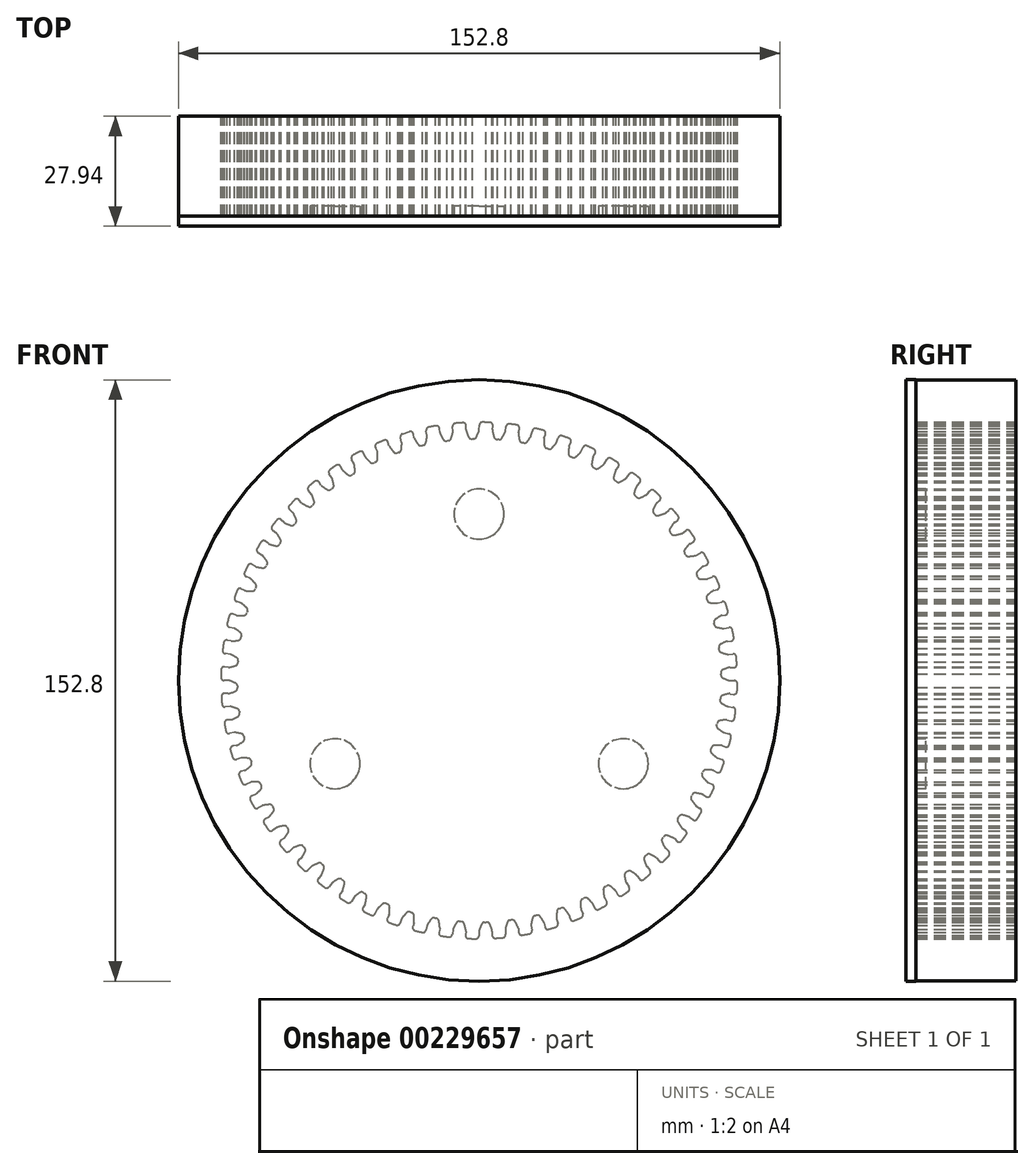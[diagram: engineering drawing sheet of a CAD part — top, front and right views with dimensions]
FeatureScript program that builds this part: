
annotation { "Feature Type Name" : "Feature", "Feature Type Description" : "" }
export const myFeature = defineFeature(function(context is Context, id is Id, definition is map)
    precondition{}
    {
        {
            var Q0;
            Q0=qCreatedBy(makeId("Front.planeOp"),FACE);
            var sketch = newSketch(context, id + "F0", { "sketchPlane" : qUnion([Q0])});
            skArc(sketch, "E0", {"start": v(-4.13, 65.49) * mm, "mid": v(-5.08, 65.42) * mm, "end": v(-6.03, 65.34) * mm});
            skPoint(sketch, "E1.orphan", {"position": v(-3.22, 59.34) * mm});
            skPoint(sketch, "E2.orphan", {"position": v(0.1, 59.43) * mm});
            skArc(sketch, "E3.MirrorCS", {"start": v(-3.28, 63.46) * mm, "mid": v(-3.01, 62.67) * mm, "end": v(-2.71, 61.9) * mm});
            skLineSegment(sketch, "E4.MirrorCS", {"start": v(-2.02, 61.41) * mm, "end": v(-1.72, 61.4) * mm});
            skLineSegment(sketch, "E5.MirrorCS", {"start": v(-1.42, 61.4) * mm, "end": v(-1.72, 61.4) * mm});
            skArc(sketch, "E6.MirrorCS", {"start": v(-0.05, 63.37) * mm, "mid": v(-0.36, 62.6) * mm, "end": v(-0.7, 61.84) * mm});
            skLineSegment(sketch, "E7.MirrorCS", {"start": v(-3.32, 63.72) * mm, "end": v(-3.3, 64.68) * mm});
            skLineSegment(sketch, "E8.MirrorCS", {"start": v(0, 63.63) * mm, "end": v(0.04, 64.84) * mm});
            skPoint(sketch, "E9.orphan", {"position": v(-2.51, 65.57) * mm});
            skPoint(sketch, "E10.MirrorCS.end.orphan", {"position": v(-3.27, 61.3) * mm});
            skPoint(sketch, "E10.MirrorCS.start.orphan", {"position": v(-3.32, 63.41) * mm});
            skPoint(sketch, "E11.end.orphan", {"position": v(0.06, 61.38) * mm});
            skPoint(sketch, "E12.trimOffspring.start.orphan", {"position": v(0, 63.5) * mm});
            skPoint(sketch, "E13.end.orphan", {"position": v(-1.72, 65.6) * mm});
            skPoint(sketch, "E13.start.orphan", {"position": v(-0.92, 65.61) * mm});
            skPoint(sketch, "E14.visualSharp", {"position": v(0.06, 65.62) * mm});
            skArc(sketch, "E14.filletArc", {"start": v(0.83, 65.61) * mm, "mid": v(0.28, 65.4) * mm, "end": v(0.04, 64.84) * mm});
            skPoint(sketch, "E15.visualSharp", {"position": v(-3.27, 65.54) * mm});
            skArc(sketch, "E15.filletArc", {"start": v(-3.3, 64.68) * mm, "mid": v(-3.54, 65.27) * mm, "end": v(-4.13, 65.49) * mm});
            skPoint(sketch, "E16.visualSharp", {"position": v(-2.51, 61.43) * mm});
            skArc(sketch, "E16.filletArc", {"start": v(-2.71, 61.9) * mm, "mid": v(-2.43, 61.55) * mm, "end": v(-2.02, 61.41) * mm});
            skPoint(sketch, "E17.visualSharp", {"position": v(-0.92, 61.39) * mm});
            skArc(sketch, "E17.filletArc", {"start": v(-1.42, 61.4) * mm, "mid": v(-1, 61.51) * mm, "end": v(-0.7, 61.84) * mm});
            skArc(sketch, "E18.filletArc", {"start": v(-0.05, 63.37) * mm, "mid": v(-0.01, 63.5) * mm, "end": v(0, 63.63) * mm});
            skPoint(sketch, "E19.visualSharp", {"position": v(-3.32, 63.59) * mm});
            skArc(sketch, "E19.filletArc", {"start": v(-3.32, 63.72) * mm, "mid": v(-3.31, 63.59) * mm, "end": v(-3.28, 63.46) * mm});
            skArc(sketch, "E20.1.0", {"start": v(-10.04, 63.98) * mm, "mid": v(-10.34, 64.54) * mm, "end": v(-10.95, 64.7) * mm});
            skLineSegment(sketch, "E20.1.1", {"start": v(-9.96, 63.02) * mm, "end": v(-10.04, 63.98) * mm});
            skArc(sketch, "E20.1.2", {"start": v(-9.96, 63.02) * mm, "mid": v(-9.94, 62.9) * mm, "end": v(-9.9, 62.77) * mm});
            skArc(sketch, "E20.1.3", {"start": v(-9.9, 62.77) * mm, "mid": v(-9.55, 62.01) * mm, "end": v(-9.17, 61.27) * mm});
            skArc(sketch, "E20.1.4", {"start": v(-9.17, 61.27) * mm, "mid": v(-8.86, 60.96) * mm, "end": v(-8.42, 60.87) * mm});
            skLineSegment(sketch, "E20.1.5", {"start": v(-8.42, 60.87) * mm, "end": v(-8.13, 60.89) * mm});
            skLineSegment(sketch, "E20.1.6", {"start": v(-7.83, 60.91) * mm, "end": v(-8.13, 60.89) * mm});
            skArc(sketch, "E20.1.7", {"start": v(-7.83, 60.91) * mm, "mid": v(-7.42, 61.07) * mm, "end": v(-7.16, 61.43) * mm});
            skArc(sketch, "E20.1.8", {"start": v(-6.67, 63.02) * mm, "mid": v(-6.9, 62.22) * mm, "end": v(-7.16, 61.43) * mm});
            skArc(sketch, "E20.1.9", {"start": v(-6.67, 63.02) * mm, "mid": v(-6.65, 63.15) * mm, "end": v(-6.65, 63.28) * mm});
            skLineSegment(sketch, "E20.1.10", {"start": v(-6.65, 63.28) * mm, "end": v(-6.74, 64.5) * mm});
            skArc(sketch, "E20.1.11", {"start": v(-6.03, 65.34) * mm, "mid": v(-6.56, 65.06) * mm, "end": v(-6.74, 64.5) * mm});
            skArc(sketch, "E20.2.0", {"start": v(-16.67, 62.58) * mm, "mid": v(-17.03, 63.1) * mm, "end": v(-17.66, 63.2) * mm});
            skLineSegment(sketch, "E20.2.1", {"start": v(-16.5, 61.64) * mm, "end": v(-16.67, 62.58) * mm});
            skArc(sketch, "E20.2.2", {"start": v(-16.5, 61.64) * mm, "mid": v(-16.46, 61.5) * mm, "end": v(-16.4, 61.4) * mm});
            skArc(sketch, "E20.2.3", {"start": v(-16.4, 61.4) * mm, "mid": v(-15.98, 60.68) * mm, "end": v(-15.52, 59.98) * mm});
            skArc(sketch, "E20.2.4", {"start": v(-15.52, 59.98) * mm, "mid": v(-15.18, 59.7) * mm, "end": v(-14.74, 59.65) * mm});
            skLineSegment(sketch, "E20.2.5", {"start": v(-14.74, 59.65) * mm, "end": v(-14.45, 59.7) * mm});
            skLineSegment(sketch, "E20.2.6", {"start": v(-14.15, 59.76) * mm, "end": v(-14.45, 59.7) * mm});
            skArc(sketch, "E20.2.7", {"start": v(-14.15, 59.76) * mm, "mid": v(-13.76, 59.96) * mm, "end": v(-13.54, 60.35) * mm});
            skArc(sketch, "E20.2.8", {"start": v(-13.22, 61.98) * mm, "mid": v(-13.36, 61.16) * mm, "end": v(-13.54, 60.35) * mm});
            skArc(sketch, "E20.2.9", {"start": v(-13.22, 61.98) * mm, "mid": v(-13.21, 62.11) * mm, "end": v(-13.23, 62.24) * mm});
            skLineSegment(sketch, "E20.2.10", {"start": v(-13.23, 62.24) * mm, "end": v(-13.45, 63.43) * mm});
            skArc(sketch, "E20.2.11", {"start": v(-12.83, 64.35) * mm, "mid": v(-13.33, 64.02) * mm, "end": v(-13.45, 63.43) * mm});
            skArc(sketch, "E20.3.0", {"start": v(-23.12, 60.5) * mm, "mid": v(-23.53, 60.98) * mm, "end": v(-24.17, 61) * mm});
            skLineSegment(sketch, "E20.3.1", {"start": v(-22.85, 59.57) * mm, "end": v(-23.12, 60.5) * mm});
            skArc(sketch, "E20.3.2", {"start": v(-22.85, 59.57) * mm, "mid": v(-22.8, 59.45) * mm, "end": v(-22.73, 59.34) * mm});
            skArc(sketch, "E20.3.3", {"start": v(-22.73, 59.34) * mm, "mid": v(-22.23, 58.67) * mm, "end": v(-21.7, 58.03) * mm});
            skArc(sketch, "E20.3.4", {"start": v(-21.7, 58.03) * mm, "mid": v(-21.34, 57.79) * mm, "end": v(-20.9, 57.78) * mm});
            skLineSegment(sketch, "E20.3.5", {"start": v(-20.9, 57.78) * mm, "end": v(-20.6, 57.87) * mm});
            skLineSegment(sketch, "E20.3.6", {"start": v(-20.32, 57.95) * mm, "end": v(-20.6, 57.87) * mm});
            skArc(sketch, "E20.3.7", {"start": v(-20.32, 57.95) * mm, "mid": v(-19.95, 58.2) * mm, "end": v(-19.78, 58.6) * mm});
            skArc(sketch, "E20.3.8", {"start": v(-19.63, 60.26) * mm, "mid": v(-19.68, 59.43) * mm, "end": v(-19.78, 58.6) * mm});
            skArc(sketch, "E20.3.9", {"start": v(-19.63, 60.26) * mm, "mid": v(-19.63, 60.39) * mm, "end": v(-19.66, 60.52) * mm});
            skLineSegment(sketch, "E20.3.10", {"start": v(-19.66, 60.52) * mm, "end": v(-20, 61.68) * mm});
            skArc(sketch, "E20.3.11", {"start": v(-19.48, 62.66) * mm, "mid": v(-19.94, 62.28) * mm, "end": v(-20, 61.68) * mm});
            skArc(sketch, "E20.4.0", {"start": v(-29.32, 57.75) * mm, "mid": v(-29.78, 58.19) * mm, "end": v(-30.4, 58.14) * mm});
            skLineSegment(sketch, "E20.4.1", {"start": v(-28.95, 56.86) * mm, "end": v(-29.32, 57.75) * mm});
            skArc(sketch, "E20.4.2", {"start": v(-28.95, 56.86) * mm, "mid": v(-28.89, 56.74) * mm, "end": v(-28.81, 56.64) * mm});
            skArc(sketch, "E20.4.3", {"start": v(-28.81, 56.64) * mm, "mid": v(-28.25, 56.03) * mm, "end": v(-27.65, 55.44) * mm});
            skArc(sketch, "E20.4.4", {"start": v(-27.65, 55.44) * mm, "mid": v(-27.26, 55.24) * mm, "end": v(-26.82, 55.28) * mm});
            skLineSegment(sketch, "E20.4.5", {"start": v(-26.82, 55.28) * mm, "end": v(-26.54, 55.4) * mm});
            skLineSegment(sketch, "E20.4.6", {"start": v(-26.27, 55.51) * mm, "end": v(-26.54, 55.4) * mm});
            skArc(sketch, "E20.4.7", {"start": v(-26.27, 55.51) * mm, "mid": v(-25.93, 55.8) * mm, "end": v(-25.8, 56.21) * mm});
            skArc(sketch, "E20.4.8", {"start": v(-25.82, 57.88) * mm, "mid": v(-25.79, 57.05) * mm, "end": v(-25.8, 56.21) * mm});
            skArc(sketch, "E20.4.9", {"start": v(-25.82, 57.88) * mm, "mid": v(-25.84, 58) * mm, "end": v(-25.88, 58.13) * mm});
            skLineSegment(sketch, "E20.4.10", {"start": v(-25.88, 58.13) * mm, "end": v(-26.34, 59.25) * mm});
            skArc(sketch, "E20.4.11", {"start": v(-25.93, 60.28) * mm, "mid": v(-26.34, 59.85) * mm, "end": v(-26.34, 59.25) * mm});
            skArc(sketch, "E20.5.0", {"start": v(-35.2, 54.37) * mm, "mid": v(-35.7, 54.76) * mm, "end": v(-36.32, 54.65) * mm});
            skLineSegment(sketch, "E20.5.1", {"start": v(-34.73, 53.52) * mm, "end": v(-35.2, 54.37) * mm});
            skArc(sketch, "E20.5.2", {"start": v(-34.73, 53.52) * mm, "mid": v(-34.66, 53.41) * mm, "end": v(-34.57, 53.32) * mm});
            skArc(sketch, "E20.5.3", {"start": v(-34.57, 53.32) * mm, "mid": v(-33.95, 52.77) * mm, "end": v(-33.3, 52.25) * mm});
            skArc(sketch, "E20.5.4", {"start": v(-33.3, 52.25) * mm, "mid": v(-32.88, 52.09) * mm, "end": v(-32.45, 52.18) * mm});
            skLineSegment(sketch, "E20.5.5", {"start": v(-32.45, 52.18) * mm, "end": v(-32.19, 52.32) * mm});
            skLineSegment(sketch, "E20.5.6", {"start": v(-31.93, 52.46) * mm, "end": v(-32.19, 52.32) * mm});
            skArc(sketch, "E20.5.7", {"start": v(-31.93, 52.46) * mm, "mid": v(-31.62, 52.78) * mm, "end": v(-31.53, 53.2) * mm});
            skArc(sketch, "E20.5.8", {"start": v(-31.73, 54.86) * mm, "mid": v(-31.6, 54.04) * mm, "end": v(-31.53, 53.2) * mm});
            skArc(sketch, "E20.5.9", {"start": v(-31.73, 54.86) * mm, "mid": v(-31.76, 54.99) * mm, "end": v(-31.81, 55.1) * mm});
            skLineSegment(sketch, "E20.5.10", {"start": v(-31.81, 55.1) * mm, "end": v(-32.4, 56.17) * mm});
            skArc(sketch, "E20.5.11", {"start": v(-32.08, 57.24) * mm, "mid": v(-32.46, 56.77) * mm, "end": v(-32.4, 56.17) * mm});
            skArc(sketch, "E20.6.0", {"start": v(-40.68, 50.4) * mm, "mid": v(-41.22, 50.72) * mm, "end": v(-41.83, 50.55) * mm});
            skLineSegment(sketch, "E20.6.1", {"start": v(-40.14, 49.6) * mm, "end": v(-40.68, 50.4) * mm});
            skArc(sketch, "E20.6.2", {"start": v(-40.14, 49.6) * mm, "mid": v(-40.06, 49.5) * mm, "end": v(-39.96, 49.4) * mm});
            skArc(sketch, "E20.6.3", {"start": v(-39.96, 49.4) * mm, "mid": v(-39.28, 48.93) * mm, "end": v(-38.58, 48.48) * mm});
            skArc(sketch, "E20.6.4", {"start": v(-38.58, 48.48) * mm, "mid": v(-38.15, 48.37) * mm, "end": v(-37.73, 48.5) * mm});
            skLineSegment(sketch, "E20.6.5", {"start": v(-37.73, 48.5) * mm, "end": v(-37.48, 48.66) * mm});
            skLineSegment(sketch, "E20.6.6", {"start": v(-37.24, 48.84) * mm, "end": v(-37.48, 48.66) * mm});
            skArc(sketch, "E20.6.7", {"start": v(-37.24, 48.84) * mm, "mid": v(-36.96, 49.18) * mm, "end": v(-36.92, 49.62) * mm});
            skArc(sketch, "E20.6.8", {"start": v(-37.29, 51.24) * mm, "mid": v(-37.08, 50.44) * mm, "end": v(-36.92, 49.62) * mm});
            skArc(sketch, "E20.6.9", {"start": v(-37.29, 51.24) * mm, "mid": v(-37.33, 51.37) * mm, "end": v(-37.4, 51.48) * mm});
            skLineSegment(sketch, "E20.6.10", {"start": v(-37.4, 51.48) * mm, "end": v(-38.09, 52.48) * mm});
            skArc(sketch, "E20.6.11", {"start": v(-37.9, 53.57) * mm, "mid": v(-38.21, 53.07) * mm, "end": v(-38.09, 52.48) * mm});
            skArc(sketch, "E20.7.0", {"start": v(-45.73, 45.86) * mm, "mid": v(-46.3, 46.14) * mm, "end": v(-46.89, 45.9) * mm});
            skLineSegment(sketch, "E20.7.1", {"start": v(-45.1, 45.13) * mm, "end": v(-45.73, 45.86) * mm});
            skArc(sketch, "E20.7.2", {"start": v(-45.1, 45.13) * mm, "mid": v(-45, 45.04) * mm, "end": v(-44.9, 44.96) * mm});
            skArc(sketch, "E20.7.3", {"start": v(-44.9, 44.96) * mm, "mid": v(-44.18, 44.56) * mm, "end": v(-43.43, 44.18) * mm});
            skArc(sketch, "E20.7.4", {"start": v(-43.43, 44.18) * mm, "mid": v(-43, 44.11) * mm, "end": v(-42.6, 44.29) * mm});
            skLineSegment(sketch, "E20.7.5", {"start": v(-42.6, 44.29) * mm, "end": v(-42.36, 44.48) * mm});
            skLineSegment(sketch, "E20.7.6", {"start": v(-42.14, 44.68) * mm, "end": v(-42.36, 44.48) * mm});
            skArc(sketch, "E20.7.7", {"start": v(-42.14, 44.68) * mm, "mid": v(-41.9, 45.05) * mm, "end": v(-41.9, 45.5) * mm});
            skArc(sketch, "E20.7.8", {"start": v(-42.44, 47.07) * mm, "mid": v(-42.15, 46.28) * mm, "end": v(-41.9, 45.5) * mm});
            skArc(sketch, "E20.7.9", {"start": v(-42.44, 47.07) * mm, "mid": v(-42.5, 47.18) * mm, "end": v(-42.57, 47.29) * mm});
            skLineSegment(sketch, "E20.7.10", {"start": v(-42.57, 47.29) * mm, "end": v(-43.36, 48.21) * mm});
            skArc(sketch, "E20.7.11", {"start": v(-43.28, 49.32) * mm, "mid": v(-43.55, 48.78) * mm, "end": v(-43.36, 48.21) * mm});
            skArc(sketch, "E20.8.0", {"start": v(-50.27, 40.83) * mm, "mid": v(-50.87, 41.05) * mm, "end": v(-51.43, 40.75) * mm});
            skLineSegment(sketch, "E20.8.1", {"start": v(-49.57, 40.17) * mm, "end": v(-50.27, 40.83) * mm});
            skArc(sketch, "E20.8.2", {"start": v(-49.57, 40.17) * mm, "mid": v(-49.47, 40.09) * mm, "end": v(-49.36, 40.02) * mm});
            skArc(sketch, "E20.8.3", {"start": v(-49.36, 40.02) * mm, "mid": v(-48.6, 39.7) * mm, "end": v(-47.81, 39.4) * mm});
            skArc(sketch, "E20.8.4", {"start": v(-47.81, 39.4) * mm, "mid": v(-47.37, 39.38) * mm, "end": v(-46.99, 39.6) * mm});
            skLineSegment(sketch, "E20.8.5", {"start": v(-46.99, 39.6) * mm, "end": v(-46.78, 39.8) * mm});
            skLineSegment(sketch, "E20.8.6", {"start": v(-46.58, 40.03) * mm, "end": v(-46.78, 39.8) * mm});
            skArc(sketch, "E20.8.7", {"start": v(-46.58, 40.03) * mm, "mid": v(-46.38, 40.42) * mm, "end": v(-46.43, 40.86) * mm});
            skArc(sketch, "E20.8.8", {"start": v(-47.13, 42.37) * mm, "mid": v(-46.76, 41.62) * mm, "end": v(-46.43, 40.86) * mm});
            skArc(sketch, "E20.8.9", {"start": v(-47.13, 42.37) * mm, "mid": v(-47.2, 42.48) * mm, "end": v(-47.28, 42.58) * mm});
            skLineSegment(sketch, "E20.8.10", {"start": v(-47.28, 42.58) * mm, "end": v(-48.17, 43.42) * mm});
            skArc(sketch, "E20.8.11", {"start": v(-48.2, 44.52) * mm, "mid": v(-48.41, 43.96) * mm, "end": v(-48.17, 43.42) * mm});
            skArc(sketch, "E20.9.0", {"start": v(-54.26, 35.35) * mm, "mid": v(-54.88, 35.5) * mm, "end": v(-55.4, 35.15) * mm});
            skLineSegment(sketch, "E20.9.1", {"start": v(-53.5, 34.77) * mm, "end": v(-54.26, 35.35) * mm});
            skArc(sketch, "E20.9.2", {"start": v(-53.5, 34.77) * mm, "mid": v(-53.4, 34.7) * mm, "end": v(-53.27, 34.64) * mm});
            skArc(sketch, "E20.9.3", {"start": v(-53.27, 34.64) * mm, "mid": v(-52.47, 34.4) * mm, "end": v(-51.67, 34.19) * mm});
            skArc(sketch, "E20.9.4", {"start": v(-51.67, 34.19) * mm, "mid": v(-51.23, 34.21) * mm, "end": v(-50.87, 34.47) * mm});
            skLineSegment(sketch, "E20.9.5", {"start": v(-50.87, 34.47) * mm, "end": v(-50.68, 34.7) * mm});
            skLineSegment(sketch, "E20.9.6", {"start": v(-50.5, 34.94) * mm, "end": v(-50.68, 34.7) * mm});
            skArc(sketch, "E20.9.7", {"start": v(-50.5, 34.94) * mm, "mid": v(-50.35, 35.35) * mm, "end": v(-50.44, 35.79) * mm});
            skArc(sketch, "E20.9.8", {"start": v(-51.3, 37.21) * mm, "mid": v(-50.86, 36.5) * mm, "end": v(-50.44, 35.79) * mm});
            skArc(sketch, "E20.9.9", {"start": v(-51.3, 37.21) * mm, "mid": v(-51.38, 37.32) * mm, "end": v(-51.48, 37.4) * mm});
            skLineSegment(sketch, "E20.9.10", {"start": v(-51.48, 37.4) * mm, "end": v(-52.44, 38.14) * mm});
            skArc(sketch, "E20.9.11", {"start": v(-52.6, 39.24) * mm, "mid": v(-52.74, 38.66) * mm, "end": v(-52.44, 38.14) * mm});
            skArc(sketch, "E20.10.0", {"start": v(-57.66, 29.49) * mm, "mid": v(-58.3, 29.57) * mm, "end": v(-58.78, 29.17) * mm});
            skLineSegment(sketch, "E20.10.1", {"start": v(-56.84, 28.98) * mm, "end": v(-57.66, 29.49) * mm});
            skArc(sketch, "E20.10.2", {"start": v(-56.84, 28.98) * mm, "mid": v(-56.72, 28.92) * mm, "end": v(-56.6, 28.89) * mm});
            skArc(sketch, "E20.10.3", {"start": v(-56.6, 28.89) * mm, "mid": v(-55.78, 28.73) * mm, "end": v(-54.96, 28.6) * mm});
            skArc(sketch, "E20.10.4", {"start": v(-54.96, 28.6) * mm, "mid": v(-54.52, 28.67) * mm, "end": v(-54.2, 28.96) * mm});
            skLineSegment(sketch, "E20.10.5", {"start": v(-54.2, 28.96) * mm, "end": v(-54.03, 29.21) * mm});
            skLineSegment(sketch, "E20.10.6", {"start": v(-53.88, 29.47) * mm, "end": v(-54.03, 29.21) * mm});
            skArc(sketch, "E20.10.7", {"start": v(-53.88, 29.47) * mm, "mid": v(-53.77, 29.9) * mm, "end": v(-53.9, 30.32) * mm});
            skArc(sketch, "E20.10.8", {"start": v(-54.9, 31.65) * mm, "mid": v(-54.4, 31) * mm, "end": v(-53.9, 30.32) * mm});
            skArc(sketch, "E20.10.9", {"start": v(-54.9, 31.65) * mm, "mid": v(-55, 31.74) * mm, "end": v(-55.1, 31.82) * mm});
            skLineSegment(sketch, "E20.10.10", {"start": v(-55.1, 31.82) * mm, "end": v(-56.14, 32.45) * mm});
            skArc(sketch, "E20.10.11", {"start": v(-56.4, 33.53) * mm, "mid": v(-56.5, 32.94) * mm, "end": v(-56.14, 32.45) * mm});
            skArc(sketch, "E20.11.0", {"start": v(-60.43, 23.3) * mm, "mid": v(-61.06, 23.32) * mm, "end": v(-61.5, 22.86) * mm});
            skLineSegment(sketch, "E20.11.1", {"start": v(-59.56, 22.88) * mm, "end": v(-60.43, 23.3) * mm});
            skArc(sketch, "E20.11.2", {"start": v(-59.56, 22.88) * mm, "mid": v(-59.44, 22.84) * mm, "end": v(-59.3, 22.81) * mm});
            skArc(sketch, "E20.11.3", {"start": v(-59.3, 22.81) * mm, "mid": v(-58.48, 22.74) * mm, "end": v(-57.65, 22.7) * mm});
            skArc(sketch, "E20.11.4", {"start": v(-57.65, 22.7) * mm, "mid": v(-57.22, 22.81) * mm, "end": v(-56.92, 23.14) * mm});
            skLineSegment(sketch, "E20.11.5", {"start": v(-56.92, 23.14) * mm, "end": v(-56.8, 23.4) * mm});
            skLineSegment(sketch, "E20.11.6", {"start": v(-56.67, 23.67) * mm, "end": v(-56.8, 23.4) * mm});
            skArc(sketch, "E20.11.7", {"start": v(-56.67, 23.67) * mm, "mid": v(-56.6, 24.11) * mm, "end": v(-56.78, 24.52) * mm});
            skArc(sketch, "E20.11.8", {"start": v(-57.91, 25.73) * mm, "mid": v(-57.33, 25.14) * mm, "end": v(-56.78, 24.52) * mm});
            skArc(sketch, "E20.11.9", {"start": v(-57.91, 25.73) * mm, "mid": v(-58.02, 25.82) * mm, "end": v(-58.13, 25.88) * mm});
            skLineSegment(sketch, "E20.11.10", {"start": v(-58.13, 25.88) * mm, "end": v(-59.22, 26.4) * mm});
            skArc(sketch, "E20.11.11", {"start": v(-59.6, 27.45) * mm, "mid": v(-59.63, 26.85) * mm, "end": v(-59.22, 26.4) * mm});
            skArc(sketch, "E20.12.0", {"start": v(-62.53, 16.85) * mm, "mid": v(-63.17, 16.8) * mm, "end": v(-63.56, 16.3) * mm});
            skLineSegment(sketch, "E20.12.1", {"start": v(-61.63, 16.53) * mm, "end": v(-62.53, 16.85) * mm});
            skArc(sketch, "E20.12.2", {"start": v(-61.63, 16.53) * mm, "mid": v(-61.5, 16.5) * mm, "end": v(-61.37, 16.49) * mm});
            skArc(sketch, "E20.12.3", {"start": v(-61.37, 16.49) * mm, "mid": v(-60.54, 16.5) * mm, "end": v(-59.7, 16.55) * mm});
            skArc(sketch, "E20.12.4", {"start": v(-59.7, 16.55) * mm, "mid": v(-59.3, 16.7) * mm, "end": v(-59.03, 17.06) * mm});
            skLineSegment(sketch, "E20.12.5", {"start": v(-59.03, 17.06) * mm, "end": v(-58.93, 17.34) * mm});
            skLineSegment(sketch, "E20.12.6", {"start": v(-58.83, 17.62) * mm, "end": v(-58.93, 17.34) * mm});
            skArc(sketch, "E20.12.7", {"start": v(-58.83, 17.62) * mm, "mid": v(-58.81, 18.06) * mm, "end": v(-59.03, 18.45) * mm});
            skArc(sketch, "E20.12.8", {"start": v(-60.29, 19.54) * mm, "mid": v(-59.65, 19) * mm, "end": v(-59.03, 18.45) * mm});
            skArc(sketch, "E20.12.9", {"start": v(-60.29, 19.54) * mm, "mid": v(-60.4, 19.61) * mm, "end": v(-60.52, 19.67) * mm});
            skLineSegment(sketch, "E20.12.10", {"start": v(-60.52, 19.67) * mm, "end": v(-61.66, 20.07) * mm});
            skArc(sketch, "E20.12.11", {"start": v(-62.14, 21.07) * mm, "mid": v(-62.1, 20.47) * mm, "end": v(-61.66, 20.07) * mm});
            skArc(sketch, "E20.13.0", {"start": v(-63.95, 10.23) * mm, "mid": v(-64.58, 10.11) * mm, "end": v(-64.91, 9.57) * mm});
            skLineSegment(sketch, "E20.13.1", {"start": v(-63.02, 10) * mm, "end": v(-63.95, 10.23) * mm});
            skArc(sketch, "E20.13.2", {"start": v(-63.02, 10) * mm, "mid": v(-62.89, 9.98) * mm, "end": v(-62.76, 9.98) * mm});
            skArc(sketch, "E20.13.3", {"start": v(-62.76, 9.98) * mm, "mid": v(-61.93, 10.08) * mm, "end": v(-61.1, 10.22) * mm});
            skArc(sketch, "E20.13.4", {"start": v(-61.1, 10.22) * mm, "mid": v(-60.71, 10.42) * mm, "end": v(-60.49, 10.8) * mm});
            skLineSegment(sketch, "E20.13.5", {"start": v(-60.49, 10.8) * mm, "end": v(-60.42, 11.09) * mm});
            skLineSegment(sketch, "E20.13.6", {"start": v(-60.35, 11.38) * mm, "end": v(-60.42, 11.09) * mm});
            skArc(sketch, "E20.13.7", {"start": v(-60.35, 11.38) * mm, "mid": v(-60.38, 11.82) * mm, "end": v(-60.64, 12.17) * mm});
            skArc(sketch, "E20.13.8", {"start": v(-62, 13.13) * mm, "mid": v(-61.3, 12.67) * mm, "end": v(-60.64, 12.17) * mm});
            skArc(sketch, "E20.13.9", {"start": v(-62, 13.13) * mm, "mid": v(-62.12, 13.2) * mm, "end": v(-62.24, 13.23) * mm});
            skLineSegment(sketch, "E20.13.10", {"start": v(-62.24, 13.23) * mm, "end": v(-63.42, 13.52) * mm});
            skArc(sketch, "E20.13.11", {"start": v(-64, 14.46) * mm, "mid": v(-63.9, 13.87) * mm, "end": v(-63.42, 13.52) * mm});
            skArc(sketch, "E20.14.0", {"start": v(-64.67, 3.48) * mm, "mid": v(-65.28, 3.3) * mm, "end": v(-65.56, 2.74) * mm});
            skLineSegment(sketch, "E20.14.1", {"start": v(-63.72, 3.36) * mm, "end": v(-64.67, 3.48) * mm});
            skArc(sketch, "E20.14.2", {"start": v(-63.72, 3.36) * mm, "mid": v(-63.59, 3.35) * mm, "end": v(-63.46, 3.37) * mm});
            skArc(sketch, "E20.14.3", {"start": v(-63.46, 3.37) * mm, "mid": v(-62.64, 3.55) * mm, "end": v(-61.84, 3.77) * mm});
            skArc(sketch, "E20.14.4", {"start": v(-61.84, 3.77) * mm, "mid": v(-61.47, 4.01) * mm, "end": v(-61.29, 4.42) * mm});
            skLineSegment(sketch, "E20.14.5", {"start": v(-61.29, 4.42) * mm, "end": v(-61.24, 4.7) * mm});
            skLineSegment(sketch, "E20.14.6", {"start": v(-61.2, 5) * mm, "end": v(-61.24, 4.7) * mm});
            skArc(sketch, "E20.14.7", {"start": v(-61.2, 5) * mm, "mid": v(-61.28, 5.44) * mm, "end": v(-61.58, 5.77) * mm});
            skArc(sketch, "E20.14.8", {"start": v(-63.03, 6.58) * mm, "mid": v(-62.3, 6.19) * mm, "end": v(-61.58, 5.77) * mm});
            skArc(sketch, "E20.14.9", {"start": v(-63.03, 6.58) * mm, "mid": v(-63.15, 6.63) * mm, "end": v(-63.28, 6.65) * mm});
            skLineSegment(sketch, "E20.14.10", {"start": v(-63.28, 6.65) * mm, "end": v(-64.49, 6.81) * mm});
            skArc(sketch, "E20.14.11", {"start": v(-65.16, 7.69) * mm, "mid": v(-65, 7.11) * mm, "end": v(-64.49, 6.81) * mm});
            skArc(sketch, "E20.15.0", {"start": v(-64.68, -3.3) * mm, "mid": v(-65.27, -3.54) * mm, "end": v(-65.49, -4.13) * mm});
            skLineSegment(sketch, "E20.15.1", {"start": v(-63.72, -3.32) * mm, "end": v(-64.68, -3.3) * mm});
            skArc(sketch, "E20.15.2", {"start": v(-63.72, -3.32) * mm, "mid": v(-63.59, -3.31) * mm, "end": v(-63.46, -3.28) * mm});
            skArc(sketch, "E20.15.3", {"start": v(-63.46, -3.28) * mm, "mid": v(-62.67, -3.01) * mm, "end": v(-61.9, -2.71) * mm});
            skArc(sketch, "E20.15.4", {"start": v(-61.9, -2.71) * mm, "mid": v(-61.55, -2.43) * mm, "end": v(-61.41, -2.02) * mm});
            skLineSegment(sketch, "E20.15.5", {"start": v(-61.41, -2.02) * mm, "end": v(-61.4, -1.72) * mm});
            skLineSegment(sketch, "E20.15.6", {"start": v(-61.4, -1.42) * mm, "end": v(-61.4, -1.72) * mm});
            skArc(sketch, "E20.15.7", {"start": v(-61.4, -1.42) * mm, "mid": v(-61.51, -1) * mm, "end": v(-61.84, -0.7) * mm});
            skArc(sketch, "E20.15.8", {"start": v(-63.37, -0.05) * mm, "mid": v(-62.6, -0.36) * mm, "end": v(-61.84, -0.7) * mm});
            skArc(sketch, "E20.15.9", {"start": v(-63.37, -0.05) * mm, "mid": v(-63.5, -0.01) * mm, "end": v(-63.63, 0) * mm});
            skLineSegment(sketch, "E20.15.10", {"start": v(-63.63, 0) * mm, "end": v(-64.84, 0.04) * mm});
            skArc(sketch, "E20.15.11", {"start": v(-65.61, 0.83) * mm, "mid": v(-65.4, 0.28) * mm, "end": v(-64.84, 0.04) * mm});
            skArc(sketch, "E20.16.0", {"start": v(-63.98, -10.04) * mm, "mid": v(-64.54, -10.34) * mm, "end": v(-64.7, -10.95) * mm});
            skLineSegment(sketch, "E20.16.1", {"start": v(-63.02, -9.96) * mm, "end": v(-63.98, -10.04) * mm});
            skArc(sketch, "E20.16.2", {"start": v(-63.02, -9.96) * mm, "mid": v(-62.9, -9.94) * mm, "end": v(-62.77, -9.9) * mm});
            skArc(sketch, "E20.16.3", {"start": v(-62.77, -9.9) * mm, "mid": v(-62.01, -9.55) * mm, "end": v(-61.27, -9.17) * mm});
            skArc(sketch, "E20.16.4", {"start": v(-61.27, -9.17) * mm, "mid": v(-60.96, -8.86) * mm, "end": v(-60.87, -8.42) * mm});
            skLineSegment(sketch, "E20.16.5", {"start": v(-60.87, -8.42) * mm, "end": v(-60.89, -8.13) * mm});
            skLineSegment(sketch, "E20.16.6", {"start": v(-60.91, -7.83) * mm, "end": v(-60.89, -8.13) * mm});
            skArc(sketch, "E20.16.7", {"start": v(-60.91, -7.83) * mm, "mid": v(-61.07, -7.42) * mm, "end": v(-61.43, -7.16) * mm});
            skArc(sketch, "E20.16.8", {"start": v(-63.02, -6.67) * mm, "mid": v(-62.22, -6.9) * mm, "end": v(-61.43, -7.16) * mm});
            skArc(sketch, "E20.16.9", {"start": v(-63.02, -6.67) * mm, "mid": v(-63.15, -6.65) * mm, "end": v(-63.28, -6.65) * mm});
            skLineSegment(sketch, "E20.16.10", {"start": v(-63.28, -6.65) * mm, "end": v(-64.5, -6.74) * mm});
            skArc(sketch, "E20.16.11", {"start": v(-65.34, -6.03) * mm, "mid": v(-65.06, -6.56) * mm, "end": v(-64.5, -6.74) * mm});
            skArc(sketch, "E20.17.0", {"start": v(-62.58, -16.67) * mm, "mid": v(-63.1, -17.03) * mm, "end": v(-63.2, -17.66) * mm});
            skLineSegment(sketch, "E20.17.1", {"start": v(-61.64, -16.5) * mm, "end": v(-62.58, -16.67) * mm});
            skArc(sketch, "E20.17.2", {"start": v(-61.64, -16.5) * mm, "mid": v(-61.5, -16.46) * mm, "end": v(-61.4, -16.4) * mm});
            skArc(sketch, "E20.17.3", {"start": v(-61.4, -16.4) * mm, "mid": v(-60.68, -15.98) * mm, "end": v(-59.98, -15.52) * mm});
            skArc(sketch, "E20.17.4", {"start": v(-59.98, -15.52) * mm, "mid": v(-59.7, -15.18) * mm, "end": v(-59.65, -14.74) * mm});
            skLineSegment(sketch, "E20.17.5", {"start": v(-59.65, -14.74) * mm, "end": v(-59.7, -14.45) * mm});
            skLineSegment(sketch, "E20.17.6", {"start": v(-59.76, -14.15) * mm, "end": v(-59.7, -14.45) * mm});
            skArc(sketch, "E20.17.7", {"start": v(-59.76, -14.15) * mm, "mid": v(-59.96, -13.76) * mm, "end": v(-60.35, -13.54) * mm});
            skArc(sketch, "E20.17.8", {"start": v(-61.98, -13.22) * mm, "mid": v(-61.16, -13.36) * mm, "end": v(-60.35, -13.54) * mm});
            skArc(sketch, "E20.17.9", {"start": v(-61.98, -13.22) * mm, "mid": v(-62.11, -13.21) * mm, "end": v(-62.24, -13.23) * mm});
            skLineSegment(sketch, "E20.17.10", {"start": v(-62.24, -13.23) * mm, "end": v(-63.43, -13.45) * mm});
            skArc(sketch, "E20.17.11", {"start": v(-64.35, -12.83) * mm, "mid": v(-64.02, -13.33) * mm, "end": v(-63.43, -13.45) * mm});
            skArc(sketch, "E20.18.0", {"start": v(-60.5, -23.12) * mm, "mid": v(-60.98, -23.53) * mm, "end": v(-61, -24.17) * mm});
            skLineSegment(sketch, "E20.18.1", {"start": v(-59.57, -22.85) * mm, "end": v(-60.5, -23.12) * mm});
            skArc(sketch, "E20.18.2", {"start": v(-59.57, -22.85) * mm, "mid": v(-59.45, -22.8) * mm, "end": v(-59.34, -22.73) * mm});
            skArc(sketch, "E20.18.3", {"start": v(-59.34, -22.73) * mm, "mid": v(-58.67, -22.23) * mm, "end": v(-58.03, -21.7) * mm});
            skArc(sketch, "E20.18.4", {"start": v(-58.03, -21.7) * mm, "mid": v(-57.79, -21.34) * mm, "end": v(-57.78, -20.9) * mm});
            skLineSegment(sketch, "E20.18.5", {"start": v(-57.78, -20.9) * mm, "end": v(-57.87, -20.6) * mm});
            skLineSegment(sketch, "E20.18.6", {"start": v(-57.95, -20.32) * mm, "end": v(-57.87, -20.6) * mm});
            skArc(sketch, "E20.18.7", {"start": v(-57.95, -20.32) * mm, "mid": v(-58.2, -19.95) * mm, "end": v(-58.6, -19.78) * mm});
            skArc(sketch, "E20.18.8", {"start": v(-60.26, -19.63) * mm, "mid": v(-59.43, -19.68) * mm, "end": v(-58.6, -19.78) * mm});
            skArc(sketch, "E20.18.9", {"start": v(-60.26, -19.63) * mm, "mid": v(-60.39, -19.63) * mm, "end": v(-60.52, -19.66) * mm});
            skLineSegment(sketch, "E20.18.10", {"start": v(-60.52, -19.66) * mm, "end": v(-61.68, -20) * mm});
            skArc(sketch, "E20.18.11", {"start": v(-62.66, -19.48) * mm, "mid": v(-62.28, -19.94) * mm, "end": v(-61.68, -20) * mm});
            skArc(sketch, "E20.19.0", {"start": v(-57.75, -29.32) * mm, "mid": v(-58.19, -29.78) * mm, "end": v(-58.14, -30.4) * mm});
            skLineSegment(sketch, "E20.19.1", {"start": v(-56.86, -28.95) * mm, "end": v(-57.75, -29.32) * mm});
            skArc(sketch, "E20.19.2", {"start": v(-56.86, -28.95) * mm, "mid": v(-56.74, -28.89) * mm, "end": v(-56.64, -28.81) * mm});
            skArc(sketch, "E20.19.3", {"start": v(-56.64, -28.81) * mm, "mid": v(-56.03, -28.25) * mm, "end": v(-55.44, -27.65) * mm});
            skArc(sketch, "E20.19.4", {"start": v(-55.44, -27.65) * mm, "mid": v(-55.24, -27.26) * mm, "end": v(-55.28, -26.82) * mm});
            skLineSegment(sketch, "E20.19.5", {"start": v(-55.28, -26.82) * mm, "end": v(-55.4, -26.54) * mm});
            skLineSegment(sketch, "E20.19.6", {"start": v(-55.51, -26.27) * mm, "end": v(-55.4, -26.54) * mm});
            skArc(sketch, "E20.19.7", {"start": v(-55.51, -26.27) * mm, "mid": v(-55.8, -25.93) * mm, "end": v(-56.21, -25.8) * mm});
            skArc(sketch, "E20.19.8", {"start": v(-57.88, -25.82) * mm, "mid": v(-57.05, -25.79) * mm, "end": v(-56.21, -25.8) * mm});
            skArc(sketch, "E20.19.9", {"start": v(-57.88, -25.82) * mm, "mid": v(-58, -25.84) * mm, "end": v(-58.13, -25.88) * mm});
            skLineSegment(sketch, "E20.19.10", {"start": v(-58.13, -25.88) * mm, "end": v(-59.25, -26.34) * mm});
            skArc(sketch, "E20.19.11", {"start": v(-60.28, -25.93) * mm, "mid": v(-59.85, -26.34) * mm, "end": v(-59.25, -26.34) * mm});
            skArc(sketch, "E20.20.0", {"start": v(-54.37, -35.2) * mm, "mid": v(-54.76, -35.7) * mm, "end": v(-54.65, -36.32) * mm});
            skLineSegment(sketch, "E20.20.1", {"start": v(-53.52, -34.73) * mm, "end": v(-54.37, -35.2) * mm});
            skArc(sketch, "E20.20.2", {"start": v(-53.52, -34.73) * mm, "mid": v(-53.41, -34.66) * mm, "end": v(-53.32, -34.57) * mm});
            skArc(sketch, "E20.20.3", {"start": v(-53.32, -34.57) * mm, "mid": v(-52.77, -33.95) * mm, "end": v(-52.25, -33.3) * mm});
            skArc(sketch, "E20.20.4", {"start": v(-52.25, -33.3) * mm, "mid": v(-52.09, -32.88) * mm, "end": v(-52.18, -32.45) * mm});
            skLineSegment(sketch, "E20.20.5", {"start": v(-52.18, -32.45) * mm, "end": v(-52.32, -32.19) * mm});
            skLineSegment(sketch, "E20.20.6", {"start": v(-52.46, -31.93) * mm, "end": v(-52.32, -32.19) * mm});
            skArc(sketch, "E20.20.7", {"start": v(-52.46, -31.93) * mm, "mid": v(-52.78, -31.62) * mm, "end": v(-53.2, -31.53) * mm});
            skArc(sketch, "E20.20.8", {"start": v(-54.86, -31.73) * mm, "mid": v(-54.04, -31.6) * mm, "end": v(-53.2, -31.53) * mm});
            skArc(sketch, "E20.20.9", {"start": v(-54.86, -31.73) * mm, "mid": v(-54.99, -31.76) * mm, "end": v(-55.1, -31.81) * mm});
            skLineSegment(sketch, "E20.20.10", {"start": v(-55.1, -31.81) * mm, "end": v(-56.17, -32.4) * mm});
            skArc(sketch, "E20.20.11", {"start": v(-57.24, -32.08) * mm, "mid": v(-56.77, -32.46) * mm, "end": v(-56.17, -32.4) * mm});
            skArc(sketch, "E20.21.0", {"start": v(-50.4, -40.68) * mm, "mid": v(-50.72, -41.22) * mm, "end": v(-50.55, -41.83) * mm});
            skLineSegment(sketch, "E20.21.1", {"start": v(-49.6, -40.14) * mm, "end": v(-50.4, -40.68) * mm});
            skArc(sketch, "E20.21.2", {"start": v(-49.6, -40.14) * mm, "mid": v(-49.5, -40.06) * mm, "end": v(-49.4, -39.96) * mm});
            skArc(sketch, "E20.21.3", {"start": v(-49.4, -39.96) * mm, "mid": v(-48.93, -39.28) * mm, "end": v(-48.48, -38.58) * mm});
            skArc(sketch, "E20.21.4", {"start": v(-48.48, -38.58) * mm, "mid": v(-48.37, -38.15) * mm, "end": v(-48.5, -37.73) * mm});
            skLineSegment(sketch, "E20.21.5", {"start": v(-48.5, -37.73) * mm, "end": v(-48.66, -37.48) * mm});
            skLineSegment(sketch, "E20.21.6", {"start": v(-48.84, -37.24) * mm, "end": v(-48.66, -37.48) * mm});
            skArc(sketch, "E20.21.7", {"start": v(-48.84, -37.24) * mm, "mid": v(-49.18, -36.96) * mm, "end": v(-49.62, -36.92) * mm});
            skArc(sketch, "E20.21.8", {"start": v(-51.24, -37.29) * mm, "mid": v(-50.44, -37.08) * mm, "end": v(-49.62, -36.92) * mm});
            skArc(sketch, "E20.21.9", {"start": v(-51.24, -37.29) * mm, "mid": v(-51.37, -37.33) * mm, "end": v(-51.48, -37.4) * mm});
            skLineSegment(sketch, "E20.21.10", {"start": v(-51.48, -37.4) * mm, "end": v(-52.48, -38.09) * mm});
            skArc(sketch, "E20.21.11", {"start": v(-53.57, -37.9) * mm, "mid": v(-53.07, -38.21) * mm, "end": v(-52.48, -38.09) * mm});
            skArc(sketch, "E20.22.0", {"start": v(-45.86, -45.73) * mm, "mid": v(-46.14, -46.3) * mm, "end": v(-45.9, -46.89) * mm});
            skLineSegment(sketch, "E20.22.1", {"start": v(-45.13, -45.1) * mm, "end": v(-45.86, -45.73) * mm});
            skArc(sketch, "E20.22.2", {"start": v(-45.13, -45.1) * mm, "mid": v(-45.04, -45) * mm, "end": v(-44.96, -44.9) * mm});
            skArc(sketch, "E20.22.3", {"start": v(-44.96, -44.9) * mm, "mid": v(-44.56, -44.18) * mm, "end": v(-44.18, -43.43) * mm});
            skArc(sketch, "E20.22.4", {"start": v(-44.18, -43.43) * mm, "mid": v(-44.11, -43) * mm, "end": v(-44.29, -42.6) * mm});
            skLineSegment(sketch, "E20.22.5", {"start": v(-44.29, -42.6) * mm, "end": v(-44.48, -42.36) * mm});
            skLineSegment(sketch, "E20.22.6", {"start": v(-44.68, -42.14) * mm, "end": v(-44.48, -42.36) * mm});
            skArc(sketch, "E20.22.7", {"start": v(-44.68, -42.14) * mm, "mid": v(-45.05, -41.9) * mm, "end": v(-45.5, -41.9) * mm});
            skArc(sketch, "E20.22.8", {"start": v(-47.07, -42.44) * mm, "mid": v(-46.28, -42.15) * mm, "end": v(-45.5, -41.9) * mm});
            skArc(sketch, "E20.22.9", {"start": v(-47.07, -42.44) * mm, "mid": v(-47.18, -42.5) * mm, "end": v(-47.29, -42.57) * mm});
            skLineSegment(sketch, "E20.22.10", {"start": v(-47.29, -42.57) * mm, "end": v(-48.21, -43.36) * mm});
            skArc(sketch, "E20.22.11", {"start": v(-49.32, -43.28) * mm, "mid": v(-48.78, -43.55) * mm, "end": v(-48.21, -43.36) * mm});
            skArc(sketch, "E20.23.0", {"start": v(-40.83, -50.27) * mm, "mid": v(-41.05, -50.87) * mm, "end": v(-40.75, -51.43) * mm});
            skLineSegment(sketch, "E20.23.1", {"start": v(-40.17, -49.57) * mm, "end": v(-40.83, -50.27) * mm});
            skArc(sketch, "E20.23.2", {"start": v(-40.17, -49.57) * mm, "mid": v(-40.09, -49.47) * mm, "end": v(-40.02, -49.36) * mm});
            skArc(sketch, "E20.23.3", {"start": v(-40.02, -49.36) * mm, "mid": v(-39.7, -48.6) * mm, "end": v(-39.4, -47.81) * mm});
            skArc(sketch, "E20.23.4", {"start": v(-39.4, -47.81) * mm, "mid": v(-39.38, -47.37) * mm, "end": v(-39.6, -46.99) * mm});
            skLineSegment(sketch, "E20.23.5", {"start": v(-39.6, -46.99) * mm, "end": v(-39.8, -46.78) * mm});
            skLineSegment(sketch, "E20.23.6", {"start": v(-40.03, -46.58) * mm, "end": v(-39.8, -46.78) * mm});
            skArc(sketch, "E20.23.7", {"start": v(-40.03, -46.58) * mm, "mid": v(-40.42, -46.38) * mm, "end": v(-40.86, -46.43) * mm});
            skArc(sketch, "E20.23.8", {"start": v(-42.37, -47.13) * mm, "mid": v(-41.62, -46.76) * mm, "end": v(-40.86, -46.43) * mm});
            skArc(sketch, "E20.23.9", {"start": v(-42.37, -47.13) * mm, "mid": v(-42.48, -47.2) * mm, "end": v(-42.58, -47.28) * mm});
            skLineSegment(sketch, "E20.23.10", {"start": v(-42.58, -47.28) * mm, "end": v(-43.42, -48.17) * mm});
            skArc(sketch, "E20.23.11", {"start": v(-44.52, -48.2) * mm, "mid": v(-43.96, -48.41) * mm, "end": v(-43.42, -48.17) * mm});
            skArc(sketch, "E20.24.0", {"start": v(-35.35, -54.26) * mm, "mid": v(-35.5, -54.88) * mm, "end": v(-35.15, -55.4) * mm});
            skLineSegment(sketch, "E20.24.1", {"start": v(-34.77, -53.5) * mm, "end": v(-35.35, -54.26) * mm});
            skArc(sketch, "E20.24.2", {"start": v(-34.77, -53.5) * mm, "mid": v(-34.7, -53.4) * mm, "end": v(-34.64, -53.27) * mm});
            skArc(sketch, "E20.24.3", {"start": v(-34.64, -53.27) * mm, "mid": v(-34.4, -52.47) * mm, "end": v(-34.19, -51.67) * mm});
            skArc(sketch, "E20.24.4", {"start": v(-34.19, -51.67) * mm, "mid": v(-34.21, -51.23) * mm, "end": v(-34.47, -50.87) * mm});
            skLineSegment(sketch, "E20.24.5", {"start": v(-34.47, -50.87) * mm, "end": v(-34.7, -50.68) * mm});
            skLineSegment(sketch, "E20.24.6", {"start": v(-34.94, -50.5) * mm, "end": v(-34.7, -50.68) * mm});
            skArc(sketch, "E20.24.7", {"start": v(-34.94, -50.5) * mm, "mid": v(-35.35, -50.35) * mm, "end": v(-35.79, -50.44) * mm});
            skArc(sketch, "E20.24.8", {"start": v(-37.21, -51.3) * mm, "mid": v(-36.5, -50.86) * mm, "end": v(-35.79, -50.44) * mm});
            skArc(sketch, "E20.24.9", {"start": v(-37.21, -51.3) * mm, "mid": v(-37.32, -51.38) * mm, "end": v(-37.4, -51.48) * mm});
            skLineSegment(sketch, "E20.24.10", {"start": v(-37.4, -51.48) * mm, "end": v(-38.14, -52.44) * mm});
            skArc(sketch, "E20.24.11", {"start": v(-39.24, -52.6) * mm, "mid": v(-38.66, -52.74) * mm, "end": v(-38.14, -52.44) * mm});
            skArc(sketch, "E20.25.0", {"start": v(-29.49, -57.66) * mm, "mid": v(-29.57, -58.3) * mm, "end": v(-29.17, -58.78) * mm});
            skLineSegment(sketch, "E20.25.1", {"start": v(-28.98, -56.84) * mm, "end": v(-29.49, -57.66) * mm});
            skArc(sketch, "E20.25.2", {"start": v(-28.98, -56.84) * mm, "mid": v(-28.92, -56.72) * mm, "end": v(-28.89, -56.6) * mm});
            skArc(sketch, "E20.25.3", {"start": v(-28.89, -56.6) * mm, "mid": v(-28.73, -55.78) * mm, "end": v(-28.6, -54.96) * mm});
            skArc(sketch, "E20.25.4", {"start": v(-28.6, -54.96) * mm, "mid": v(-28.67, -54.52) * mm, "end": v(-28.96, -54.2) * mm});
            skLineSegment(sketch, "E20.25.5", {"start": v(-28.96, -54.2) * mm, "end": v(-29.21, -54.03) * mm});
            skLineSegment(sketch, "E20.25.6", {"start": v(-29.47, -53.88) * mm, "end": v(-29.21, -54.03) * mm});
            skArc(sketch, "E20.25.7", {"start": v(-29.47, -53.88) * mm, "mid": v(-29.9, -53.77) * mm, "end": v(-30.32, -53.9) * mm});
            skArc(sketch, "E20.25.8", {"start": v(-31.65, -54.9) * mm, "mid": v(-31, -54.4) * mm, "end": v(-30.32, -53.9) * mm});
            skArc(sketch, "E20.25.9", {"start": v(-31.65, -54.9) * mm, "mid": v(-31.74, -55) * mm, "end": v(-31.82, -55.1) * mm});
            skLineSegment(sketch, "E20.25.10", {"start": v(-31.82, -55.1) * mm, "end": v(-32.45, -56.14) * mm});
            skArc(sketch, "E20.25.11", {"start": v(-33.53, -56.4) * mm, "mid": v(-32.94, -56.5) * mm, "end": v(-32.45, -56.14) * mm});
            skArc(sketch, "E20.26.0", {"start": v(-23.3, -60.43) * mm, "mid": v(-23.32, -61.06) * mm, "end": v(-22.86, -61.5) * mm});
            skLineSegment(sketch, "E20.26.1", {"start": v(-22.88, -59.56) * mm, "end": v(-23.3, -60.43) * mm});
            skArc(sketch, "E20.26.2", {"start": v(-22.88, -59.56) * mm, "mid": v(-22.84, -59.44) * mm, "end": v(-22.81, -59.3) * mm});
            skArc(sketch, "E20.26.3", {"start": v(-22.81, -59.3) * mm, "mid": v(-22.74, -58.48) * mm, "end": v(-22.7, -57.65) * mm});
            skArc(sketch, "E20.26.4", {"start": v(-22.7, -57.65) * mm, "mid": v(-22.81, -57.22) * mm, "end": v(-23.14, -56.92) * mm});
            skLineSegment(sketch, "E20.26.5", {"start": v(-23.14, -56.92) * mm, "end": v(-23.4, -56.8) * mm});
            skLineSegment(sketch, "E20.26.6", {"start": v(-23.67, -56.67) * mm, "end": v(-23.4, -56.8) * mm});
            skArc(sketch, "E20.26.7", {"start": v(-23.67, -56.67) * mm, "mid": v(-24.11, -56.6) * mm, "end": v(-24.52, -56.78) * mm});
            skArc(sketch, "E20.26.8", {"start": v(-25.73, -57.91) * mm, "mid": v(-25.14, -57.33) * mm, "end": v(-24.52, -56.78) * mm});
            skArc(sketch, "E20.26.9", {"start": v(-25.73, -57.91) * mm, "mid": v(-25.82, -58.02) * mm, "end": v(-25.88, -58.13) * mm});
            skLineSegment(sketch, "E20.26.10", {"start": v(-25.88, -58.13) * mm, "end": v(-26.4, -59.22) * mm});
            skArc(sketch, "E20.26.11", {"start": v(-27.45, -59.6) * mm, "mid": v(-26.85, -59.63) * mm, "end": v(-26.4, -59.22) * mm});
            skArc(sketch, "E20.27.0", {"start": v(-16.85, -62.53) * mm, "mid": v(-16.8, -63.17) * mm, "end": v(-16.3, -63.56) * mm});
            skLineSegment(sketch, "E20.27.1", {"start": v(-16.53, -61.63) * mm, "end": v(-16.85, -62.53) * mm});
            skArc(sketch, "E20.27.2", {"start": v(-16.53, -61.63) * mm, "mid": v(-16.5, -61.5) * mm, "end": v(-16.49, -61.37) * mm});
            skArc(sketch, "E20.27.3", {"start": v(-16.49, -61.37) * mm, "mid": v(-16.5, -60.54) * mm, "end": v(-16.55, -59.7) * mm});
            skArc(sketch, "E20.27.4", {"start": v(-16.55, -59.7) * mm, "mid": v(-16.7, -59.3) * mm, "end": v(-17.06, -59.03) * mm});
            skLineSegment(sketch, "E20.27.5", {"start": v(-17.06, -59.03) * mm, "end": v(-17.34, -58.93) * mm});
            skLineSegment(sketch, "E20.27.6", {"start": v(-17.62, -58.83) * mm, "end": v(-17.34, -58.93) * mm});
            skArc(sketch, "E20.27.7", {"start": v(-17.62, -58.83) * mm, "mid": v(-18.06, -58.81) * mm, "end": v(-18.45, -59.03) * mm});
            skArc(sketch, "E20.27.8", {"start": v(-19.54, -60.29) * mm, "mid": v(-19, -59.65) * mm, "end": v(-18.45, -59.03) * mm});
            skArc(sketch, "E20.27.9", {"start": v(-19.54, -60.29) * mm, "mid": v(-19.61, -60.4) * mm, "end": v(-19.67, -60.52) * mm});
            skLineSegment(sketch, "E20.27.10", {"start": v(-19.67, -60.52) * mm, "end": v(-20.07, -61.66) * mm});
            skArc(sketch, "E20.27.11", {"start": v(-21.07, -62.14) * mm, "mid": v(-20.47, -62.1) * mm, "end": v(-20.07, -61.66) * mm});
            skArc(sketch, "E20.28.0", {"start": v(-10.23, -63.95) * mm, "mid": v(-10.11, -64.58) * mm, "end": v(-9.57, -64.91) * mm});
            skLineSegment(sketch, "E20.28.1", {"start": v(-10, -63.02) * mm, "end": v(-10.23, -63.95) * mm});
            skArc(sketch, "E20.28.2", {"start": v(-10, -63.02) * mm, "mid": v(-9.98, -62.89) * mm, "end": v(-9.98, -62.76) * mm});
            skArc(sketch, "E20.28.3", {"start": v(-9.98, -62.76) * mm, "mid": v(-10.08, -61.93) * mm, "end": v(-10.22, -61.1) * mm});
            skArc(sketch, "E20.28.4", {"start": v(-10.22, -61.1) * mm, "mid": v(-10.42, -60.71) * mm, "end": v(-10.8, -60.49) * mm});
            skLineSegment(sketch, "E20.28.5", {"start": v(-10.8, -60.49) * mm, "end": v(-11.09, -60.42) * mm});
            skLineSegment(sketch, "E20.28.6", {"start": v(-11.38, -60.35) * mm, "end": v(-11.09, -60.42) * mm});
            skArc(sketch, "E20.28.7", {"start": v(-11.38, -60.35) * mm, "mid": v(-11.82, -60.38) * mm, "end": v(-12.17, -60.64) * mm});
            skArc(sketch, "E20.28.8", {"start": v(-13.13, -62) * mm, "mid": v(-12.67, -61.3) * mm, "end": v(-12.17, -60.64) * mm});
            skArc(sketch, "E20.28.9", {"start": v(-13.13, -62) * mm, "mid": v(-13.2, -62.12) * mm, "end": v(-13.23, -62.24) * mm});
            skLineSegment(sketch, "E20.28.10", {"start": v(-13.23, -62.24) * mm, "end": v(-13.52, -63.42) * mm});
            skArc(sketch, "E20.28.11", {"start": v(-14.46, -64) * mm, "mid": v(-13.87, -63.9) * mm, "end": v(-13.52, -63.42) * mm});
            skArc(sketch, "E20.29.0", {"start": v(-3.48, -64.67) * mm, "mid": v(-3.3, -65.28) * mm, "end": v(-2.74, -65.56) * mm});
            skLineSegment(sketch, "E20.29.1", {"start": v(-3.36, -63.72) * mm, "end": v(-3.48, -64.67) * mm});
            skArc(sketch, "E20.29.2", {"start": v(-3.36, -63.72) * mm, "mid": v(-3.35, -63.59) * mm, "end": v(-3.37, -63.46) * mm});
            skArc(sketch, "E20.29.3", {"start": v(-3.37, -63.46) * mm, "mid": v(-3.55, -62.64) * mm, "end": v(-3.77, -61.84) * mm});
            skArc(sketch, "E20.29.4", {"start": v(-3.77, -61.84) * mm, "mid": v(-4.01, -61.47) * mm, "end": v(-4.42, -61.29) * mm});
            skLineSegment(sketch, "E20.29.5", {"start": v(-4.42, -61.29) * mm, "end": v(-4.7, -61.24) * mm});
            skLineSegment(sketch, "E20.29.6", {"start": v(-5, -61.2) * mm, "end": v(-4.7, -61.24) * mm});
            skArc(sketch, "E20.29.7", {"start": v(-5, -61.2) * mm, "mid": v(-5.44, -61.28) * mm, "end": v(-5.77, -61.58) * mm});
            skArc(sketch, "E20.29.8", {"start": v(-6.58, -63.03) * mm, "mid": v(-6.19, -62.3) * mm, "end": v(-5.77, -61.58) * mm});
            skArc(sketch, "E20.29.9", {"start": v(-6.58, -63.03) * mm, "mid": v(-6.63, -63.15) * mm, "end": v(-6.65, -63.28) * mm});
            skLineSegment(sketch, "E20.29.10", {"start": v(-6.65, -63.28) * mm, "end": v(-6.81, -64.49) * mm});
            skArc(sketch, "E20.29.11", {"start": v(-7.69, -65.16) * mm, "mid": v(-7.11, -65) * mm, "end": v(-6.81, -64.49) * mm});
            skArc(sketch, "E20.30.0", {"start": v(3.3, -64.68) * mm, "mid": v(3.54, -65.27) * mm, "end": v(4.13, -65.49) * mm});
            skLineSegment(sketch, "E20.30.1", {"start": v(3.32, -63.72) * mm, "end": v(3.3, -64.68) * mm});
            skArc(sketch, "E20.30.2", {"start": v(3.32, -63.72) * mm, "mid": v(3.31, -63.59) * mm, "end": v(3.28, -63.46) * mm});
            skArc(sketch, "E20.30.3", {"start": v(3.28, -63.46) * mm, "mid": v(3.01, -62.67) * mm, "end": v(2.71, -61.9) * mm});
            skArc(sketch, "E20.30.4", {"start": v(2.71, -61.9) * mm, "mid": v(2.43, -61.55) * mm, "end": v(2.02, -61.41) * mm});
            skLineSegment(sketch, "E20.30.5", {"start": v(2.02, -61.41) * mm, "end": v(1.72, -61.4) * mm});
            skLineSegment(sketch, "E20.30.6", {"start": v(1.42, -61.4) * mm, "end": v(1.72, -61.4) * mm});
            skArc(sketch, "E20.30.7", {"start": v(1.42, -61.4) * mm, "mid": v(1, -61.51) * mm, "end": v(0.7, -61.84) * mm});
            skArc(sketch, "E20.30.8", {"start": v(0.05, -63.37) * mm, "mid": v(0.36, -62.6) * mm, "end": v(0.7, -61.84) * mm});
            skArc(sketch, "E20.30.9", {"start": v(0.05, -63.37) * mm, "mid": v(0.01, -63.5) * mm, "end": v(0, -63.63) * mm});
            skLineSegment(sketch, "E20.30.10", {"start": v(0, -63.63) * mm, "end": v(-0.04, -64.84) * mm});
            skArc(sketch, "E20.30.11", {"start": v(-0.83, -65.61) * mm, "mid": v(-0.28, -65.4) * mm, "end": v(-0.04, -64.84) * mm});
            skArc(sketch, "E20.31.0", {"start": v(10.04, -63.98) * mm, "mid": v(10.34, -64.54) * mm, "end": v(10.95, -64.7) * mm});
            skLineSegment(sketch, "E20.31.1", {"start": v(9.96, -63.02) * mm, "end": v(10.04, -63.98) * mm});
            skArc(sketch, "E20.31.2", {"start": v(9.96, -63.02) * mm, "mid": v(9.94, -62.9) * mm, "end": v(9.9, -62.77) * mm});
            skArc(sketch, "E20.31.3", {"start": v(9.9, -62.77) * mm, "mid": v(9.55, -62.01) * mm, "end": v(9.17, -61.27) * mm});
            skArc(sketch, "E20.31.4", {"start": v(9.17, -61.27) * mm, "mid": v(8.86, -60.96) * mm, "end": v(8.42, -60.87) * mm});
            skLineSegment(sketch, "E20.31.5", {"start": v(8.42, -60.87) * mm, "end": v(8.13, -60.89) * mm});
            skLineSegment(sketch, "E20.31.6", {"start": v(7.83, -60.91) * mm, "end": v(8.13, -60.89) * mm});
            skArc(sketch, "E20.31.7", {"start": v(7.83, -60.91) * mm, "mid": v(7.42, -61.07) * mm, "end": v(7.16, -61.43) * mm});
            skArc(sketch, "E20.31.8", {"start": v(6.67, -63.02) * mm, "mid": v(6.9, -62.22) * mm, "end": v(7.16, -61.43) * mm});
            skArc(sketch, "E20.31.9", {"start": v(6.67, -63.02) * mm, "mid": v(6.65, -63.15) * mm, "end": v(6.65, -63.28) * mm});
            skLineSegment(sketch, "E20.31.10", {"start": v(6.65, -63.28) * mm, "end": v(6.74, -64.5) * mm});
            skArc(sketch, "E20.31.11", {"start": v(6.03, -65.34) * mm, "mid": v(6.56, -65.06) * mm, "end": v(6.74, -64.5) * mm});
            skArc(sketch, "E20.32.0", {"start": v(16.67, -62.58) * mm, "mid": v(17.03, -63.1) * mm, "end": v(17.66, -63.2) * mm});
            skLineSegment(sketch, "E20.32.1", {"start": v(16.5, -61.64) * mm, "end": v(16.67, -62.58) * mm});
            skArc(sketch, "E20.32.2", {"start": v(16.5, -61.64) * mm, "mid": v(16.46, -61.5) * mm, "end": v(16.4, -61.4) * mm});
            skArc(sketch, "E20.32.3", {"start": v(16.4, -61.4) * mm, "mid": v(15.98, -60.68) * mm, "end": v(15.52, -59.98) * mm});
            skArc(sketch, "E20.32.4", {"start": v(15.52, -59.98) * mm, "mid": v(15.18, -59.7) * mm, "end": v(14.74, -59.65) * mm});
            skLineSegment(sketch, "E20.32.5", {"start": v(14.74, -59.65) * mm, "end": v(14.45, -59.7) * mm});
            skLineSegment(sketch, "E20.32.6", {"start": v(14.15, -59.76) * mm, "end": v(14.45, -59.7) * mm});
            skArc(sketch, "E20.32.7", {"start": v(14.15, -59.76) * mm, "mid": v(13.76, -59.96) * mm, "end": v(13.54, -60.35) * mm});
            skArc(sketch, "E20.32.8", {"start": v(13.22, -61.98) * mm, "mid": v(13.36, -61.16) * mm, "end": v(13.54, -60.35) * mm});
            skArc(sketch, "E20.32.9", {"start": v(13.22, -61.98) * mm, "mid": v(13.21, -62.11) * mm, "end": v(13.23, -62.24) * mm});
            skLineSegment(sketch, "E20.32.10", {"start": v(13.23, -62.24) * mm, "end": v(13.45, -63.43) * mm});
            skArc(sketch, "E20.32.11", {"start": v(12.83, -64.35) * mm, "mid": v(13.33, -64.02) * mm, "end": v(13.45, -63.43) * mm});
            skArc(sketch, "E20.33.0", {"start": v(23.12, -60.5) * mm, "mid": v(23.53, -60.98) * mm, "end": v(24.17, -61) * mm});
            skLineSegment(sketch, "E20.33.1", {"start": v(22.85, -59.57) * mm, "end": v(23.12, -60.5) * mm});
            skArc(sketch, "E20.33.2", {"start": v(22.85, -59.57) * mm, "mid": v(22.8, -59.45) * mm, "end": v(22.73, -59.34) * mm});
            skArc(sketch, "E20.33.3", {"start": v(22.73, -59.34) * mm, "mid": v(22.23, -58.67) * mm, "end": v(21.7, -58.03) * mm});
            skArc(sketch, "E20.33.4", {"start": v(21.7, -58.03) * mm, "mid": v(21.34, -57.79) * mm, "end": v(20.9, -57.78) * mm});
            skLineSegment(sketch, "E20.33.5", {"start": v(20.9, -57.78) * mm, "end": v(20.6, -57.87) * mm});
            skLineSegment(sketch, "E20.33.6", {"start": v(20.32, -57.95) * mm, "end": v(20.6, -57.87) * mm});
            skArc(sketch, "E20.33.7", {"start": v(20.32, -57.95) * mm, "mid": v(19.95, -58.2) * mm, "end": v(19.78, -58.6) * mm});
            skArc(sketch, "E20.33.8", {"start": v(19.63, -60.26) * mm, "mid": v(19.68, -59.43) * mm, "end": v(19.78, -58.6) * mm});
            skArc(sketch, "E20.33.9", {"start": v(19.63, -60.26) * mm, "mid": v(19.63, -60.39) * mm, "end": v(19.66, -60.52) * mm});
            skLineSegment(sketch, "E20.33.10", {"start": v(19.66, -60.52) * mm, "end": v(20, -61.68) * mm});
            skArc(sketch, "E20.33.11", {"start": v(19.48, -62.66) * mm, "mid": v(19.94, -62.28) * mm, "end": v(20, -61.68) * mm});
            skArc(sketch, "E20.34.0", {"start": v(29.32, -57.75) * mm, "mid": v(29.78, -58.19) * mm, "end": v(30.4, -58.14) * mm});
            skLineSegment(sketch, "E20.34.1", {"start": v(28.95, -56.86) * mm, "end": v(29.32, -57.75) * mm});
            skArc(sketch, "E20.34.2", {"start": v(28.95, -56.86) * mm, "mid": v(28.89, -56.74) * mm, "end": v(28.81, -56.64) * mm});
            skArc(sketch, "E20.34.3", {"start": v(28.81, -56.64) * mm, "mid": v(28.25, -56.03) * mm, "end": v(27.65, -55.44) * mm});
            skArc(sketch, "E20.34.4", {"start": v(27.65, -55.44) * mm, "mid": v(27.26, -55.24) * mm, "end": v(26.82, -55.28) * mm});
            skLineSegment(sketch, "E20.34.5", {"start": v(26.82, -55.28) * mm, "end": v(26.54, -55.4) * mm});
            skLineSegment(sketch, "E20.34.6", {"start": v(26.27, -55.51) * mm, "end": v(26.54, -55.4) * mm});
            skArc(sketch, "E20.34.7", {"start": v(26.27, -55.51) * mm, "mid": v(25.93, -55.8) * mm, "end": v(25.8, -56.21) * mm});
            skArc(sketch, "E20.34.8", {"start": v(25.82, -57.88) * mm, "mid": v(25.79, -57.05) * mm, "end": v(25.8, -56.21) * mm});
            skArc(sketch, "E20.34.9", {"start": v(25.82, -57.88) * mm, "mid": v(25.84, -58) * mm, "end": v(25.88, -58.13) * mm});
            skLineSegment(sketch, "E20.34.10", {"start": v(25.88, -58.13) * mm, "end": v(26.34, -59.25) * mm});
            skArc(sketch, "E20.34.11", {"start": v(25.93, -60.28) * mm, "mid": v(26.34, -59.85) * mm, "end": v(26.34, -59.25) * mm});
            skArc(sketch, "E20.35.0", {"start": v(35.2, -54.37) * mm, "mid": v(35.7, -54.76) * mm, "end": v(36.32, -54.65) * mm});
            skLineSegment(sketch, "E20.35.1", {"start": v(34.73, -53.52) * mm, "end": v(35.2, -54.37) * mm});
            skArc(sketch, "E20.35.2", {"start": v(34.73, -53.52) * mm, "mid": v(34.66, -53.41) * mm, "end": v(34.57, -53.32) * mm});
            skArc(sketch, "E20.35.3", {"start": v(34.57, -53.32) * mm, "mid": v(33.95, -52.77) * mm, "end": v(33.3, -52.25) * mm});
            skArc(sketch, "E20.35.4", {"start": v(33.3, -52.25) * mm, "mid": v(32.88, -52.09) * mm, "end": v(32.45, -52.18) * mm});
            skLineSegment(sketch, "E20.35.5", {"start": v(32.45, -52.18) * mm, "end": v(32.19, -52.32) * mm});
            skLineSegment(sketch, "E20.35.6", {"start": v(31.93, -52.46) * mm, "end": v(32.19, -52.32) * mm});
            skArc(sketch, "E20.35.7", {"start": v(31.93, -52.46) * mm, "mid": v(31.62, -52.78) * mm, "end": v(31.53, -53.2) * mm});
            skArc(sketch, "E20.35.8", {"start": v(31.73, -54.86) * mm, "mid": v(31.6, -54.04) * mm, "end": v(31.53, -53.2) * mm});
            skArc(sketch, "E20.35.9", {"start": v(31.73, -54.86) * mm, "mid": v(31.76, -54.99) * mm, "end": v(31.81, -55.1) * mm});
            skLineSegment(sketch, "E20.35.10", {"start": v(31.81, -55.1) * mm, "end": v(32.4, -56.17) * mm});
            skArc(sketch, "E20.35.11", {"start": v(32.08, -57.24) * mm, "mid": v(32.46, -56.77) * mm, "end": v(32.4, -56.17) * mm});
            skArc(sketch, "E20.36.0", {"start": v(40.68, -50.4) * mm, "mid": v(41.22, -50.72) * mm, "end": v(41.83, -50.55) * mm});
            skLineSegment(sketch, "E20.36.1", {"start": v(40.14, -49.6) * mm, "end": v(40.68, -50.4) * mm});
            skArc(sketch, "E20.36.2", {"start": v(40.14, -49.6) * mm, "mid": v(40.06, -49.5) * mm, "end": v(39.96, -49.4) * mm});
            skArc(sketch, "E20.36.3", {"start": v(39.96, -49.4) * mm, "mid": v(39.28, -48.93) * mm, "end": v(38.58, -48.48) * mm});
            skArc(sketch, "E20.36.4", {"start": v(38.58, -48.48) * mm, "mid": v(38.15, -48.37) * mm, "end": v(37.73, -48.5) * mm});
            skLineSegment(sketch, "E20.36.5", {"start": v(37.73, -48.5) * mm, "end": v(37.48, -48.66) * mm});
            skLineSegment(sketch, "E20.36.6", {"start": v(37.24, -48.84) * mm, "end": v(37.48, -48.66) * mm});
            skArc(sketch, "E20.36.7", {"start": v(37.24, -48.84) * mm, "mid": v(36.96, -49.18) * mm, "end": v(36.92, -49.62) * mm});
            skArc(sketch, "E20.36.8", {"start": v(37.29, -51.24) * mm, "mid": v(37.08, -50.44) * mm, "end": v(36.92, -49.62) * mm});
            skArc(sketch, "E20.36.9", {"start": v(37.29, -51.24) * mm, "mid": v(37.33, -51.37) * mm, "end": v(37.4, -51.48) * mm});
            skLineSegment(sketch, "E20.36.10", {"start": v(37.4, -51.48) * mm, "end": v(38.09, -52.48) * mm});
            skArc(sketch, "E20.36.11", {"start": v(37.9, -53.57) * mm, "mid": v(38.21, -53.07) * mm, "end": v(38.09, -52.48) * mm});
            skArc(sketch, "E20.37.0", {"start": v(45.73, -45.86) * mm, "mid": v(46.3, -46.14) * mm, "end": v(46.89, -45.9) * mm});
            skLineSegment(sketch, "E20.37.1", {"start": v(45.1, -45.13) * mm, "end": v(45.73, -45.86) * mm});
            skArc(sketch, "E20.37.2", {"start": v(45.1, -45.13) * mm, "mid": v(45, -45.04) * mm, "end": v(44.9, -44.96) * mm});
            skArc(sketch, "E20.37.3", {"start": v(44.9, -44.96) * mm, "mid": v(44.18, -44.56) * mm, "end": v(43.43, -44.18) * mm});
            skArc(sketch, "E20.37.4", {"start": v(43.43, -44.18) * mm, "mid": v(43, -44.11) * mm, "end": v(42.6, -44.29) * mm});
            skLineSegment(sketch, "E20.37.5", {"start": v(42.6, -44.29) * mm, "end": v(42.36, -44.48) * mm});
            skLineSegment(sketch, "E20.37.6", {"start": v(42.14, -44.68) * mm, "end": v(42.36, -44.48) * mm});
            skArc(sketch, "E20.37.7", {"start": v(42.14, -44.68) * mm, "mid": v(41.9, -45.05) * mm, "end": v(41.9, -45.5) * mm});
            skArc(sketch, "E20.37.8", {"start": v(42.44, -47.07) * mm, "mid": v(42.15, -46.28) * mm, "end": v(41.9, -45.5) * mm});
            skArc(sketch, "E20.37.9", {"start": v(42.44, -47.07) * mm, "mid": v(42.5, -47.18) * mm, "end": v(42.57, -47.29) * mm});
            skLineSegment(sketch, "E20.37.10", {"start": v(42.57, -47.29) * mm, "end": v(43.36, -48.21) * mm});
            skArc(sketch, "E20.37.11", {"start": v(43.28, -49.32) * mm, "mid": v(43.55, -48.78) * mm, "end": v(43.36, -48.21) * mm});
            skArc(sketch, "E20.38.0", {"start": v(50.27, -40.83) * mm, "mid": v(50.87, -41.05) * mm, "end": v(51.43, -40.75) * mm});
            skLineSegment(sketch, "E20.38.1", {"start": v(49.57, -40.17) * mm, "end": v(50.27, -40.83) * mm});
            skArc(sketch, "E20.38.2", {"start": v(49.57, -40.17) * mm, "mid": v(49.47, -40.09) * mm, "end": v(49.36, -40.02) * mm});
            skArc(sketch, "E20.38.3", {"start": v(49.36, -40.02) * mm, "mid": v(48.6, -39.7) * mm, "end": v(47.81, -39.4) * mm});
            skArc(sketch, "E20.38.4", {"start": v(47.81, -39.4) * mm, "mid": v(47.37, -39.38) * mm, "end": v(46.99, -39.6) * mm});
            skLineSegment(sketch, "E20.38.5", {"start": v(46.99, -39.6) * mm, "end": v(46.78, -39.8) * mm});
            skLineSegment(sketch, "E20.38.6", {"start": v(46.58, -40.03) * mm, "end": v(46.78, -39.8) * mm});
            skArc(sketch, "E20.38.7", {"start": v(46.58, -40.03) * mm, "mid": v(46.38, -40.42) * mm, "end": v(46.43, -40.86) * mm});
            skArc(sketch, "E20.38.8", {"start": v(47.13, -42.37) * mm, "mid": v(46.76, -41.62) * mm, "end": v(46.43, -40.86) * mm});
            skArc(sketch, "E20.38.9", {"start": v(47.13, -42.37) * mm, "mid": v(47.2, -42.48) * mm, "end": v(47.28, -42.58) * mm});
            skLineSegment(sketch, "E20.38.10", {"start": v(47.28, -42.58) * mm, "end": v(48.17, -43.42) * mm});
            skArc(sketch, "E20.38.11", {"start": v(48.2, -44.52) * mm, "mid": v(48.41, -43.96) * mm, "end": v(48.17, -43.42) * mm});
            skArc(sketch, "E20.39.0", {"start": v(54.26, -35.35) * mm, "mid": v(54.88, -35.5) * mm, "end": v(55.4, -35.15) * mm});
            skLineSegment(sketch, "E20.39.1", {"start": v(53.5, -34.77) * mm, "end": v(54.26, -35.35) * mm});
            skArc(sketch, "E20.39.2", {"start": v(53.5, -34.77) * mm, "mid": v(53.4, -34.7) * mm, "end": v(53.27, -34.64) * mm});
            skArc(sketch, "E20.39.3", {"start": v(53.27, -34.64) * mm, "mid": v(52.47, -34.4) * mm, "end": v(51.67, -34.19) * mm});
            skArc(sketch, "E20.39.4", {"start": v(51.67, -34.19) * mm, "mid": v(51.23, -34.21) * mm, "end": v(50.87, -34.47) * mm});
            skLineSegment(sketch, "E20.39.5", {"start": v(50.87, -34.47) * mm, "end": v(50.68, -34.7) * mm});
            skLineSegment(sketch, "E20.39.6", {"start": v(50.5, -34.94) * mm, "end": v(50.68, -34.7) * mm});
            skArc(sketch, "E20.39.7", {"start": v(50.5, -34.94) * mm, "mid": v(50.35, -35.35) * mm, "end": v(50.44, -35.79) * mm});
            skArc(sketch, "E20.39.8", {"start": v(51.3, -37.21) * mm, "mid": v(50.86, -36.5) * mm, "end": v(50.44, -35.79) * mm});
            skArc(sketch, "E20.39.9", {"start": v(51.3, -37.21) * mm, "mid": v(51.38, -37.32) * mm, "end": v(51.48, -37.4) * mm});
            skLineSegment(sketch, "E20.39.10", {"start": v(51.48, -37.4) * mm, "end": v(52.44, -38.14) * mm});
            skArc(sketch, "E20.39.11", {"start": v(52.6, -39.24) * mm, "mid": v(52.74, -38.66) * mm, "end": v(52.44, -38.14) * mm});
            skArc(sketch, "E20.40.0", {"start": v(57.66, -29.49) * mm, "mid": v(58.3, -29.57) * mm, "end": v(58.78, -29.17) * mm});
            skLineSegment(sketch, "E20.40.1", {"start": v(56.84, -28.98) * mm, "end": v(57.66, -29.49) * mm});
            skArc(sketch, "E20.40.2", {"start": v(56.84, -28.98) * mm, "mid": v(56.72, -28.92) * mm, "end": v(56.6, -28.89) * mm});
            skArc(sketch, "E20.40.3", {"start": v(56.6, -28.89) * mm, "mid": v(55.78, -28.73) * mm, "end": v(54.96, -28.6) * mm});
            skArc(sketch, "E20.40.4", {"start": v(54.96, -28.6) * mm, "mid": v(54.52, -28.67) * mm, "end": v(54.2, -28.96) * mm});
            skLineSegment(sketch, "E20.40.5", {"start": v(54.2, -28.96) * mm, "end": v(54.03, -29.21) * mm});
            skLineSegment(sketch, "E20.40.6", {"start": v(53.88, -29.47) * mm, "end": v(54.03, -29.21) * mm});
            skArc(sketch, "E20.40.7", {"start": v(53.88, -29.47) * mm, "mid": v(53.77, -29.9) * mm, "end": v(53.9, -30.32) * mm});
            skArc(sketch, "E20.40.8", {"start": v(54.9, -31.65) * mm, "mid": v(54.4, -31) * mm, "end": v(53.9, -30.32) * mm});
            skArc(sketch, "E20.40.9", {"start": v(54.9, -31.65) * mm, "mid": v(55, -31.74) * mm, "end": v(55.1, -31.82) * mm});
            skLineSegment(sketch, "E20.40.10", {"start": v(55.1, -31.82) * mm, "end": v(56.14, -32.45) * mm});
            skArc(sketch, "E20.40.11", {"start": v(56.4, -33.53) * mm, "mid": v(56.5, -32.94) * mm, "end": v(56.14, -32.45) * mm});
            skArc(sketch, "E20.41.0", {"start": v(60.43, -23.3) * mm, "mid": v(61.06, -23.32) * mm, "end": v(61.5, -22.86) * mm});
            skLineSegment(sketch, "E20.41.1", {"start": v(59.56, -22.88) * mm, "end": v(60.43, -23.3) * mm});
            skArc(sketch, "E20.41.2", {"start": v(59.56, -22.88) * mm, "mid": v(59.44, -22.84) * mm, "end": v(59.3, -22.81) * mm});
            skArc(sketch, "E20.41.3", {"start": v(59.3, -22.81) * mm, "mid": v(58.48, -22.74) * mm, "end": v(57.65, -22.7) * mm});
            skArc(sketch, "E20.41.4", {"start": v(57.65, -22.7) * mm, "mid": v(57.22, -22.81) * mm, "end": v(56.92, -23.14) * mm});
            skLineSegment(sketch, "E20.41.5", {"start": v(56.92, -23.14) * mm, "end": v(56.8, -23.4) * mm});
            skLineSegment(sketch, "E20.41.6", {"start": v(56.67, -23.67) * mm, "end": v(56.8, -23.4) * mm});
            skArc(sketch, "E20.41.7", {"start": v(56.67, -23.67) * mm, "mid": v(56.6, -24.11) * mm, "end": v(56.78, -24.52) * mm});
            skArc(sketch, "E20.41.8", {"start": v(57.91, -25.73) * mm, "mid": v(57.33, -25.14) * mm, "end": v(56.78, -24.52) * mm});
            skArc(sketch, "E20.41.9", {"start": v(57.91, -25.73) * mm, "mid": v(58.02, -25.82) * mm, "end": v(58.13, -25.88) * mm});
            skLineSegment(sketch, "E20.41.10", {"start": v(58.13, -25.88) * mm, "end": v(59.22, -26.4) * mm});
            skArc(sketch, "E20.41.11", {"start": v(59.6, -27.45) * mm, "mid": v(59.63, -26.85) * mm, "end": v(59.22, -26.4) * mm});
            skArc(sketch, "E20.42.0", {"start": v(62.53, -16.85) * mm, "mid": v(63.17, -16.8) * mm, "end": v(63.56, -16.3) * mm});
            skLineSegment(sketch, "E20.42.1", {"start": v(61.63, -16.53) * mm, "end": v(62.53, -16.85) * mm});
            skArc(sketch, "E20.42.2", {"start": v(61.63, -16.53) * mm, "mid": v(61.5, -16.5) * mm, "end": v(61.37, -16.49) * mm});
            skArc(sketch, "E20.42.3", {"start": v(61.37, -16.49) * mm, "mid": v(60.54, -16.5) * mm, "end": v(59.7, -16.55) * mm});
            skArc(sketch, "E20.42.4", {"start": v(59.7, -16.55) * mm, "mid": v(59.3, -16.7) * mm, "end": v(59.03, -17.06) * mm});
            skLineSegment(sketch, "E20.42.5", {"start": v(59.03, -17.06) * mm, "end": v(58.93, -17.34) * mm});
            skLineSegment(sketch, "E20.42.6", {"start": v(58.83, -17.62) * mm, "end": v(58.93, -17.34) * mm});
            skArc(sketch, "E20.42.7", {"start": v(58.83, -17.62) * mm, "mid": v(58.81, -18.06) * mm, "end": v(59.03, -18.45) * mm});
            skArc(sketch, "E20.42.8", {"start": v(60.29, -19.54) * mm, "mid": v(59.65, -19) * mm, "end": v(59.03, -18.45) * mm});
            skArc(sketch, "E20.42.9", {"start": v(60.29, -19.54) * mm, "mid": v(60.4, -19.61) * mm, "end": v(60.52, -19.67) * mm});
            skLineSegment(sketch, "E20.42.10", {"start": v(60.52, -19.67) * mm, "end": v(61.66, -20.07) * mm});
            skArc(sketch, "E20.42.11", {"start": v(62.14, -21.07) * mm, "mid": v(62.1, -20.47) * mm, "end": v(61.66, -20.07) * mm});
            skArc(sketch, "E20.43.0", {"start": v(63.95, -10.23) * mm, "mid": v(64.58, -10.11) * mm, "end": v(64.91, -9.57) * mm});
            skLineSegment(sketch, "E20.43.1", {"start": v(63.02, -10) * mm, "end": v(63.95, -10.23) * mm});
            skArc(sketch, "E20.43.2", {"start": v(63.02, -10) * mm, "mid": v(62.89, -9.98) * mm, "end": v(62.76, -9.98) * mm});
            skArc(sketch, "E20.43.3", {"start": v(62.76, -9.98) * mm, "mid": v(61.93, -10.08) * mm, "end": v(61.1, -10.22) * mm});
            skArc(sketch, "E20.43.4", {"start": v(61.1, -10.22) * mm, "mid": v(60.71, -10.42) * mm, "end": v(60.49, -10.8) * mm});
            skLineSegment(sketch, "E20.43.5", {"start": v(60.49, -10.8) * mm, "end": v(60.42, -11.09) * mm});
            skLineSegment(sketch, "E20.43.6", {"start": v(60.35, -11.38) * mm, "end": v(60.42, -11.09) * mm});
            skArc(sketch, "E20.43.7", {"start": v(60.35, -11.38) * mm, "mid": v(60.38, -11.82) * mm, "end": v(60.64, -12.17) * mm});
            skArc(sketch, "E20.43.8", {"start": v(62, -13.13) * mm, "mid": v(61.3, -12.67) * mm, "end": v(60.64, -12.17) * mm});
            skArc(sketch, "E20.43.9", {"start": v(62, -13.13) * mm, "mid": v(62.12, -13.2) * mm, "end": v(62.24, -13.23) * mm});
            skLineSegment(sketch, "E20.43.10", {"start": v(62.24, -13.23) * mm, "end": v(63.42, -13.52) * mm});
            skArc(sketch, "E20.43.11", {"start": v(64, -14.46) * mm, "mid": v(63.9, -13.87) * mm, "end": v(63.42, -13.52) * mm});
            skArc(sketch, "E20.44.0", {"start": v(64.67, -3.48) * mm, "mid": v(65.28, -3.3) * mm, "end": v(65.56, -2.74) * mm});
            skLineSegment(sketch, "E20.44.1", {"start": v(63.72, -3.36) * mm, "end": v(64.67, -3.48) * mm});
            skArc(sketch, "E20.44.2", {"start": v(63.72, -3.36) * mm, "mid": v(63.59, -3.35) * mm, "end": v(63.46, -3.37) * mm});
            skArc(sketch, "E20.44.3", {"start": v(63.46, -3.37) * mm, "mid": v(62.64, -3.55) * mm, "end": v(61.84, -3.77) * mm});
            skArc(sketch, "E20.44.4", {"start": v(61.84, -3.77) * mm, "mid": v(61.47, -4.01) * mm, "end": v(61.29, -4.42) * mm});
            skLineSegment(sketch, "E20.44.5", {"start": v(61.29, -4.42) * mm, "end": v(61.24, -4.7) * mm});
            skLineSegment(sketch, "E20.44.6", {"start": v(61.2, -5) * mm, "end": v(61.24, -4.7) * mm});
            skArc(sketch, "E20.44.7", {"start": v(61.2, -5) * mm, "mid": v(61.28, -5.44) * mm, "end": v(61.58, -5.77) * mm});
            skArc(sketch, "E20.44.8", {"start": v(63.03, -6.58) * mm, "mid": v(62.3, -6.19) * mm, "end": v(61.58, -5.77) * mm});
            skArc(sketch, "E20.44.9", {"start": v(63.03, -6.58) * mm, "mid": v(63.15, -6.63) * mm, "end": v(63.28, -6.65) * mm});
            skLineSegment(sketch, "E20.44.10", {"start": v(63.28, -6.65) * mm, "end": v(64.49, -6.81) * mm});
            skArc(sketch, "E20.44.11", {"start": v(65.16, -7.69) * mm, "mid": v(65, -7.11) * mm, "end": v(64.49, -6.81) * mm});
            skArc(sketch, "E20.45.0", {"start": v(64.68, 3.3) * mm, "mid": v(65.27, 3.54) * mm, "end": v(65.49, 4.13) * mm});
            skLineSegment(sketch, "E20.45.1", {"start": v(63.72, 3.32) * mm, "end": v(64.68, 3.3) * mm});
            skArc(sketch, "E20.45.2", {"start": v(63.72, 3.32) * mm, "mid": v(63.59, 3.31) * mm, "end": v(63.46, 3.28) * mm});
            skArc(sketch, "E20.45.3", {"start": v(63.46, 3.28) * mm, "mid": v(62.67, 3.01) * mm, "end": v(61.9, 2.71) * mm});
            skArc(sketch, "E20.45.4", {"start": v(61.9, 2.71) * mm, "mid": v(61.55, 2.43) * mm, "end": v(61.41, 2.02) * mm});
            skLineSegment(sketch, "E20.45.5", {"start": v(61.41, 2.02) * mm, "end": v(61.4, 1.72) * mm});
            skLineSegment(sketch, "E20.45.6", {"start": v(61.4, 1.42) * mm, "end": v(61.4, 1.72) * mm});
            skArc(sketch, "E20.45.7", {"start": v(61.4, 1.42) * mm, "mid": v(61.51, 1) * mm, "end": v(61.84, 0.7) * mm});
            skArc(sketch, "E20.45.8", {"start": v(63.37, 0.05) * mm, "mid": v(62.6, 0.36) * mm, "end": v(61.84, 0.7) * mm});
            skArc(sketch, "E20.45.9", {"start": v(63.37, 0.05) * mm, "mid": v(63.5, 0.01) * mm, "end": v(63.63, 0) * mm});
            skLineSegment(sketch, "E20.45.10", {"start": v(63.63, 0) * mm, "end": v(64.84, -0.04) * mm});
            skArc(sketch, "E20.45.11", {"start": v(65.61, -0.83) * mm, "mid": v(65.4, -0.28) * mm, "end": v(64.84, -0.04) * mm});
            skArc(sketch, "E20.46.0", {"start": v(63.98, 10.04) * mm, "mid": v(64.54, 10.34) * mm, "end": v(64.7, 10.95) * mm});
            skLineSegment(sketch, "E20.46.1", {"start": v(63.02, 9.96) * mm, "end": v(63.98, 10.04) * mm});
            skArc(sketch, "E20.46.2", {"start": v(63.02, 9.96) * mm, "mid": v(62.9, 9.94) * mm, "end": v(62.77, 9.9) * mm});
            skArc(sketch, "E20.46.3", {"start": v(62.77, 9.9) * mm, "mid": v(62.01, 9.55) * mm, "end": v(61.27, 9.17) * mm});
            skArc(sketch, "E20.46.4", {"start": v(61.27, 9.17) * mm, "mid": v(60.96, 8.86) * mm, "end": v(60.87, 8.42) * mm});
            skLineSegment(sketch, "E20.46.5", {"start": v(60.87, 8.42) * mm, "end": v(60.89, 8.13) * mm});
            skLineSegment(sketch, "E20.46.6", {"start": v(60.91, 7.83) * mm, "end": v(60.89, 8.13) * mm});
            skArc(sketch, "E20.46.7", {"start": v(60.91, 7.83) * mm, "mid": v(61.07, 7.42) * mm, "end": v(61.43, 7.16) * mm});
            skArc(sketch, "E20.46.8", {"start": v(63.02, 6.67) * mm, "mid": v(62.22, 6.9) * mm, "end": v(61.43, 7.16) * mm});
            skArc(sketch, "E20.46.9", {"start": v(63.02, 6.67) * mm, "mid": v(63.15, 6.65) * mm, "end": v(63.28, 6.65) * mm});
            skLineSegment(sketch, "E20.46.10", {"start": v(63.28, 6.65) * mm, "end": v(64.5, 6.74) * mm});
            skArc(sketch, "E20.46.11", {"start": v(65.34, 6.03) * mm, "mid": v(65.06, 6.56) * mm, "end": v(64.5, 6.74) * mm});
            skArc(sketch, "E20.47.0", {"start": v(62.58, 16.67) * mm, "mid": v(63.1, 17.03) * mm, "end": v(63.2, 17.66) * mm});
            skLineSegment(sketch, "E20.47.1", {"start": v(61.64, 16.5) * mm, "end": v(62.58, 16.67) * mm});
            skArc(sketch, "E20.47.2", {"start": v(61.64, 16.5) * mm, "mid": v(61.5, 16.46) * mm, "end": v(61.4, 16.4) * mm});
            skArc(sketch, "E20.47.3", {"start": v(61.4, 16.4) * mm, "mid": v(60.68, 15.98) * mm, "end": v(59.98, 15.52) * mm});
            skArc(sketch, "E20.47.4", {"start": v(59.98, 15.52) * mm, "mid": v(59.7, 15.18) * mm, "end": v(59.65, 14.74) * mm});
            skLineSegment(sketch, "E20.47.5", {"start": v(59.65, 14.74) * mm, "end": v(59.7, 14.45) * mm});
            skLineSegment(sketch, "E20.47.6", {"start": v(59.76, 14.15) * mm, "end": v(59.7, 14.45) * mm});
            skArc(sketch, "E20.47.7", {"start": v(59.76, 14.15) * mm, "mid": v(59.96, 13.76) * mm, "end": v(60.35, 13.54) * mm});
            skArc(sketch, "E20.47.8", {"start": v(61.98, 13.22) * mm, "mid": v(61.16, 13.36) * mm, "end": v(60.35, 13.54) * mm});
            skArc(sketch, "E20.47.9", {"start": v(61.98, 13.22) * mm, "mid": v(62.11, 13.21) * mm, "end": v(62.24, 13.23) * mm});
            skLineSegment(sketch, "E20.47.10", {"start": v(62.24, 13.23) * mm, "end": v(63.43, 13.45) * mm});
            skArc(sketch, "E20.47.11", {"start": v(64.35, 12.83) * mm, "mid": v(64.02, 13.33) * mm, "end": v(63.43, 13.45) * mm});
            skArc(sketch, "E20.48.0", {"start": v(60.5, 23.12) * mm, "mid": v(60.98, 23.53) * mm, "end": v(61, 24.17) * mm});
            skLineSegment(sketch, "E20.48.1", {"start": v(59.57, 22.85) * mm, "end": v(60.5, 23.12) * mm});
            skArc(sketch, "E20.48.2", {"start": v(59.57, 22.85) * mm, "mid": v(59.45, 22.8) * mm, "end": v(59.34, 22.73) * mm});
            skArc(sketch, "E20.48.3", {"start": v(59.34, 22.73) * mm, "mid": v(58.67, 22.23) * mm, "end": v(58.03, 21.7) * mm});
            skArc(sketch, "E20.48.4", {"start": v(58.03, 21.7) * mm, "mid": v(57.79, 21.34) * mm, "end": v(57.78, 20.9) * mm});
            skLineSegment(sketch, "E20.48.5", {"start": v(57.78, 20.9) * mm, "end": v(57.87, 20.6) * mm});
            skLineSegment(sketch, "E20.48.6", {"start": v(57.95, 20.32) * mm, "end": v(57.87, 20.6) * mm});
            skArc(sketch, "E20.48.7", {"start": v(57.95, 20.32) * mm, "mid": v(58.2, 19.95) * mm, "end": v(58.6, 19.78) * mm});
            skArc(sketch, "E20.48.8", {"start": v(60.26, 19.63) * mm, "mid": v(59.43, 19.68) * mm, "end": v(58.6, 19.78) * mm});
            skArc(sketch, "E20.48.9", {"start": v(60.26, 19.63) * mm, "mid": v(60.39, 19.63) * mm, "end": v(60.52, 19.66) * mm});
            skLineSegment(sketch, "E20.48.10", {"start": v(60.52, 19.66) * mm, "end": v(61.68, 20) * mm});
            skArc(sketch, "E20.48.11", {"start": v(62.66, 19.48) * mm, "mid": v(62.28, 19.94) * mm, "end": v(61.68, 20) * mm});
            skArc(sketch, "E20.49.0", {"start": v(57.75, 29.32) * mm, "mid": v(58.19, 29.78) * mm, "end": v(58.14, 30.4) * mm});
            skLineSegment(sketch, "E20.49.1", {"start": v(56.86, 28.95) * mm, "end": v(57.75, 29.32) * mm});
            skArc(sketch, "E20.49.2", {"start": v(56.86, 28.95) * mm, "mid": v(56.74, 28.89) * mm, "end": v(56.64, 28.81) * mm});
            skArc(sketch, "E20.49.3", {"start": v(56.64, 28.81) * mm, "mid": v(56.03, 28.25) * mm, "end": v(55.44, 27.65) * mm});
            skArc(sketch, "E20.49.4", {"start": v(55.44, 27.65) * mm, "mid": v(55.24, 27.26) * mm, "end": v(55.28, 26.82) * mm});
            skLineSegment(sketch, "E20.49.5", {"start": v(55.28, 26.82) * mm, "end": v(55.4, 26.54) * mm});
            skLineSegment(sketch, "E20.49.6", {"start": v(55.51, 26.27) * mm, "end": v(55.4, 26.54) * mm});
            skArc(sketch, "E20.49.7", {"start": v(55.51, 26.27) * mm, "mid": v(55.8, 25.93) * mm, "end": v(56.21, 25.8) * mm});
            skArc(sketch, "E20.49.8", {"start": v(57.88, 25.82) * mm, "mid": v(57.05, 25.79) * mm, "end": v(56.21, 25.8) * mm});
            skArc(sketch, "E20.49.9", {"start": v(57.88, 25.82) * mm, "mid": v(58, 25.84) * mm, "end": v(58.13, 25.88) * mm});
            skLineSegment(sketch, "E20.49.10", {"start": v(58.13, 25.88) * mm, "end": v(59.25, 26.34) * mm});
            skArc(sketch, "E20.49.11", {"start": v(60.28, 25.93) * mm, "mid": v(59.85, 26.34) * mm, "end": v(59.25, 26.34) * mm});
            skArc(sketch, "E20.50.0", {"start": v(54.37, 35.2) * mm, "mid": v(54.76, 35.7) * mm, "end": v(54.65, 36.32) * mm});
            skLineSegment(sketch, "E20.50.1", {"start": v(53.52, 34.73) * mm, "end": v(54.37, 35.2) * mm});
            skArc(sketch, "E20.50.2", {"start": v(53.52, 34.73) * mm, "mid": v(53.41, 34.66) * mm, "end": v(53.32, 34.57) * mm});
            skArc(sketch, "E20.50.3", {"start": v(53.32, 34.57) * mm, "mid": v(52.77, 33.95) * mm, "end": v(52.25, 33.3) * mm});
            skArc(sketch, "E20.50.4", {"start": v(52.25, 33.3) * mm, "mid": v(52.09, 32.88) * mm, "end": v(52.18, 32.45) * mm});
            skLineSegment(sketch, "E20.50.5", {"start": v(52.18, 32.45) * mm, "end": v(52.32, 32.19) * mm});
            skLineSegment(sketch, "E20.50.6", {"start": v(52.46, 31.93) * mm, "end": v(52.32, 32.19) * mm});
            skArc(sketch, "E20.50.7", {"start": v(52.46, 31.93) * mm, "mid": v(52.78, 31.62) * mm, "end": v(53.2, 31.53) * mm});
            skArc(sketch, "E20.50.8", {"start": v(54.86, 31.73) * mm, "mid": v(54.04, 31.6) * mm, "end": v(53.2, 31.53) * mm});
            skArc(sketch, "E20.50.9", {"start": v(54.86, 31.73) * mm, "mid": v(54.99, 31.76) * mm, "end": v(55.1, 31.81) * mm});
            skLineSegment(sketch, "E20.50.10", {"start": v(55.1, 31.81) * mm, "end": v(56.17, 32.4) * mm});
            skArc(sketch, "E20.50.11", {"start": v(57.24, 32.08) * mm, "mid": v(56.77, 32.46) * mm, "end": v(56.17, 32.4) * mm});
            skArc(sketch, "E20.51.0", {"start": v(50.4, 40.68) * mm, "mid": v(50.72, 41.22) * mm, "end": v(50.55, 41.83) * mm});
            skLineSegment(sketch, "E20.51.1", {"start": v(49.6, 40.14) * mm, "end": v(50.4, 40.68) * mm});
            skArc(sketch, "E20.51.2", {"start": v(49.6, 40.14) * mm, "mid": v(49.5, 40.06) * mm, "end": v(49.4, 39.96) * mm});
            skArc(sketch, "E20.51.3", {"start": v(49.4, 39.96) * mm, "mid": v(48.93, 39.28) * mm, "end": v(48.48, 38.58) * mm});
            skArc(sketch, "E20.51.4", {"start": v(48.48, 38.58) * mm, "mid": v(48.37, 38.15) * mm, "end": v(48.5, 37.73) * mm});
            skLineSegment(sketch, "E20.51.5", {"start": v(48.5, 37.73) * mm, "end": v(48.66, 37.48) * mm});
            skLineSegment(sketch, "E20.51.6", {"start": v(48.84, 37.24) * mm, "end": v(48.66, 37.48) * mm});
            skArc(sketch, "E20.51.7", {"start": v(48.84, 37.24) * mm, "mid": v(49.18, 36.96) * mm, "end": v(49.62, 36.92) * mm});
            skArc(sketch, "E20.51.8", {"start": v(51.24, 37.29) * mm, "mid": v(50.44, 37.08) * mm, "end": v(49.62, 36.92) * mm});
            skArc(sketch, "E20.51.9", {"start": v(51.24, 37.29) * mm, "mid": v(51.37, 37.33) * mm, "end": v(51.48, 37.4) * mm});
            skLineSegment(sketch, "E20.51.10", {"start": v(51.48, 37.4) * mm, "end": v(52.48, 38.09) * mm});
            skArc(sketch, "E20.51.11", {"start": v(53.57, 37.9) * mm, "mid": v(53.07, 38.21) * mm, "end": v(52.48, 38.09) * mm});
            skArc(sketch, "E20.52.0", {"start": v(45.86, 45.73) * mm, "mid": v(46.14, 46.3) * mm, "end": v(45.9, 46.89) * mm});
            skLineSegment(sketch, "E20.52.1", {"start": v(45.13, 45.1) * mm, "end": v(45.86, 45.73) * mm});
            skArc(sketch, "E20.52.2", {"start": v(45.13, 45.1) * mm, "mid": v(45.04, 45) * mm, "end": v(44.96, 44.9) * mm});
            skArc(sketch, "E20.52.3", {"start": v(44.96, 44.9) * mm, "mid": v(44.56, 44.18) * mm, "end": v(44.18, 43.43) * mm});
            skArc(sketch, "E20.52.4", {"start": v(44.18, 43.43) * mm, "mid": v(44.11, 43) * mm, "end": v(44.29, 42.6) * mm});
            skLineSegment(sketch, "E20.52.5", {"start": v(44.29, 42.6) * mm, "end": v(44.48, 42.36) * mm});
            skLineSegment(sketch, "E20.52.6", {"start": v(44.68, 42.14) * mm, "end": v(44.48, 42.36) * mm});
            skArc(sketch, "E20.52.7", {"start": v(44.68, 42.14) * mm, "mid": v(45.05, 41.9) * mm, "end": v(45.5, 41.9) * mm});
            skArc(sketch, "E20.52.8", {"start": v(47.07, 42.44) * mm, "mid": v(46.28, 42.15) * mm, "end": v(45.5, 41.9) * mm});
            skArc(sketch, "E20.52.9", {"start": v(47.07, 42.44) * mm, "mid": v(47.18, 42.5) * mm, "end": v(47.29, 42.57) * mm});
            skLineSegment(sketch, "E20.52.10", {"start": v(47.29, 42.57) * mm, "end": v(48.21, 43.36) * mm});
            skArc(sketch, "E20.52.11", {"start": v(49.32, 43.28) * mm, "mid": v(48.78, 43.55) * mm, "end": v(48.21, 43.36) * mm});
            skArc(sketch, "E20.53.0", {"start": v(40.83, 50.27) * mm, "mid": v(41.05, 50.87) * mm, "end": v(40.75, 51.43) * mm});
            skLineSegment(sketch, "E20.53.1", {"start": v(40.17, 49.57) * mm, "end": v(40.83, 50.27) * mm});
            skArc(sketch, "E20.53.2", {"start": v(40.17, 49.57) * mm, "mid": v(40.09, 49.47) * mm, "end": v(40.02, 49.36) * mm});
            skArc(sketch, "E20.53.3", {"start": v(40.02, 49.36) * mm, "mid": v(39.7, 48.6) * mm, "end": v(39.4, 47.81) * mm});
            skArc(sketch, "E20.53.4", {"start": v(39.4, 47.81) * mm, "mid": v(39.38, 47.37) * mm, "end": v(39.6, 46.99) * mm});
            skLineSegment(sketch, "E20.53.5", {"start": v(39.6, 46.99) * mm, "end": v(39.8, 46.78) * mm});
            skLineSegment(sketch, "E20.53.6", {"start": v(40.03, 46.58) * mm, "end": v(39.8, 46.78) * mm});
            skArc(sketch, "E20.53.7", {"start": v(40.03, 46.58) * mm, "mid": v(40.42, 46.38) * mm, "end": v(40.86, 46.43) * mm});
            skArc(sketch, "E20.53.8", {"start": v(42.37, 47.13) * mm, "mid": v(41.62, 46.76) * mm, "end": v(40.86, 46.43) * mm});
            skArc(sketch, "E20.53.9", {"start": v(42.37, 47.13) * mm, "mid": v(42.48, 47.2) * mm, "end": v(42.58, 47.28) * mm});
            skLineSegment(sketch, "E20.53.10", {"start": v(42.58, 47.28) * mm, "end": v(43.42, 48.17) * mm});
            skArc(sketch, "E20.53.11", {"start": v(44.52, 48.2) * mm, "mid": v(43.96, 48.41) * mm, "end": v(43.42, 48.17) * mm});
            skArc(sketch, "E20.54.0", {"start": v(35.35, 54.26) * mm, "mid": v(35.5, 54.88) * mm, "end": v(35.15, 55.4) * mm});
            skLineSegment(sketch, "E20.54.1", {"start": v(34.77, 53.5) * mm, "end": v(35.35, 54.26) * mm});
            skArc(sketch, "E20.54.2", {"start": v(34.77, 53.5) * mm, "mid": v(34.7, 53.4) * mm, "end": v(34.64, 53.27) * mm});
            skArc(sketch, "E20.54.3", {"start": v(34.64, 53.27) * mm, "mid": v(34.4, 52.47) * mm, "end": v(34.19, 51.67) * mm});
            skArc(sketch, "E20.54.4", {"start": v(34.19, 51.67) * mm, "mid": v(34.21, 51.23) * mm, "end": v(34.47, 50.87) * mm});
            skLineSegment(sketch, "E20.54.5", {"start": v(34.47, 50.87) * mm, "end": v(34.7, 50.68) * mm});
            skLineSegment(sketch, "E20.54.6", {"start": v(34.94, 50.5) * mm, "end": v(34.7, 50.68) * mm});
            skArc(sketch, "E20.54.7", {"start": v(34.94, 50.5) * mm, "mid": v(35.35, 50.35) * mm, "end": v(35.79, 50.44) * mm});
            skArc(sketch, "E20.54.8", {"start": v(37.21, 51.3) * mm, "mid": v(36.5, 50.86) * mm, "end": v(35.79, 50.44) * mm});
            skArc(sketch, "E20.54.9", {"start": v(37.21, 51.3) * mm, "mid": v(37.32, 51.38) * mm, "end": v(37.4, 51.48) * mm});
            skLineSegment(sketch, "E20.54.10", {"start": v(37.4, 51.48) * mm, "end": v(38.14, 52.44) * mm});
            skArc(sketch, "E20.54.11", {"start": v(39.24, 52.6) * mm, "mid": v(38.66, 52.74) * mm, "end": v(38.14, 52.44) * mm});
            skArc(sketch, "E20.55.0", {"start": v(29.49, 57.66) * mm, "mid": v(29.57, 58.3) * mm, "end": v(29.17, 58.78) * mm});
            skLineSegment(sketch, "E20.55.1", {"start": v(28.98, 56.84) * mm, "end": v(29.49, 57.66) * mm});
            skArc(sketch, "E20.55.2", {"start": v(28.98, 56.84) * mm, "mid": v(28.92, 56.72) * mm, "end": v(28.89, 56.6) * mm});
            skArc(sketch, "E20.55.3", {"start": v(28.89, 56.6) * mm, "mid": v(28.73, 55.78) * mm, "end": v(28.6, 54.96) * mm});
            skArc(sketch, "E20.55.4", {"start": v(28.6, 54.96) * mm, "mid": v(28.67, 54.52) * mm, "end": v(28.96, 54.2) * mm});
            skLineSegment(sketch, "E20.55.5", {"start": v(28.96, 54.2) * mm, "end": v(29.21, 54.03) * mm});
            skLineSegment(sketch, "E20.55.6", {"start": v(29.47, 53.88) * mm, "end": v(29.21, 54.03) * mm});
            skArc(sketch, "E20.55.7", {"start": v(29.47, 53.88) * mm, "mid": v(29.9, 53.77) * mm, "end": v(30.32, 53.9) * mm});
            skArc(sketch, "E20.55.8", {"start": v(31.65, 54.9) * mm, "mid": v(31, 54.4) * mm, "end": v(30.32, 53.9) * mm});
            skArc(sketch, "E20.55.9", {"start": v(31.65, 54.9) * mm, "mid": v(31.74, 55) * mm, "end": v(31.82, 55.1) * mm});
            skLineSegment(sketch, "E20.55.10", {"start": v(31.82, 55.1) * mm, "end": v(32.45, 56.14) * mm});
            skArc(sketch, "E20.55.11", {"start": v(33.53, 56.4) * mm, "mid": v(32.94, 56.5) * mm, "end": v(32.45, 56.14) * mm});
            skArc(sketch, "E20.56.0", {"start": v(23.3, 60.43) * mm, "mid": v(23.32, 61.06) * mm, "end": v(22.86, 61.5) * mm});
            skLineSegment(sketch, "E20.56.1", {"start": v(22.88, 59.56) * mm, "end": v(23.3, 60.43) * mm});
            skArc(sketch, "E20.56.2", {"start": v(22.88, 59.56) * mm, "mid": v(22.84, 59.44) * mm, "end": v(22.81, 59.3) * mm});
            skArc(sketch, "E20.56.3", {"start": v(22.81, 59.3) * mm, "mid": v(22.74, 58.48) * mm, "end": v(22.7, 57.65) * mm});
            skArc(sketch, "E20.56.4", {"start": v(22.7, 57.65) * mm, "mid": v(22.81, 57.22) * mm, "end": v(23.14, 56.92) * mm});
            skLineSegment(sketch, "E20.56.5", {"start": v(23.14, 56.92) * mm, "end": v(23.4, 56.8) * mm});
            skLineSegment(sketch, "E20.56.6", {"start": v(23.67, 56.67) * mm, "end": v(23.4, 56.8) * mm});
            skArc(sketch, "E20.56.7", {"start": v(23.67, 56.67) * mm, "mid": v(24.11, 56.6) * mm, "end": v(24.52, 56.78) * mm});
            skArc(sketch, "E20.56.8", {"start": v(25.73, 57.91) * mm, "mid": v(25.14, 57.33) * mm, "end": v(24.52, 56.78) * mm});
            skArc(sketch, "E20.56.9", {"start": v(25.73, 57.91) * mm, "mid": v(25.82, 58.02) * mm, "end": v(25.88, 58.13) * mm});
            skLineSegment(sketch, "E20.56.10", {"start": v(25.88, 58.13) * mm, "end": v(26.4, 59.22) * mm});
            skArc(sketch, "E20.56.11", {"start": v(27.45, 59.6) * mm, "mid": v(26.85, 59.63) * mm, "end": v(26.4, 59.22) * mm});
            skArc(sketch, "E20.57.0", {"start": v(16.85, 62.53) * mm, "mid": v(16.8, 63.17) * mm, "end": v(16.3, 63.56) * mm});
            skLineSegment(sketch, "E20.57.1", {"start": v(16.53, 61.63) * mm, "end": v(16.85, 62.53) * mm});
            skArc(sketch, "E20.57.2", {"start": v(16.53, 61.63) * mm, "mid": v(16.5, 61.5) * mm, "end": v(16.49, 61.37) * mm});
            skArc(sketch, "E20.57.3", {"start": v(16.49, 61.37) * mm, "mid": v(16.5, 60.54) * mm, "end": v(16.55, 59.7) * mm});
            skArc(sketch, "E20.57.4", {"start": v(16.55, 59.7) * mm, "mid": v(16.7, 59.3) * mm, "end": v(17.06, 59.03) * mm});
            skLineSegment(sketch, "E20.57.5", {"start": v(17.06, 59.03) * mm, "end": v(17.34, 58.93) * mm});
            skLineSegment(sketch, "E20.57.6", {"start": v(17.62, 58.83) * mm, "end": v(17.34, 58.93) * mm});
            skArc(sketch, "E20.57.7", {"start": v(17.62, 58.83) * mm, "mid": v(18.06, 58.81) * mm, "end": v(18.45, 59.03) * mm});
            skArc(sketch, "E20.57.8", {"start": v(19.54, 60.29) * mm, "mid": v(19, 59.65) * mm, "end": v(18.45, 59.03) * mm});
            skArc(sketch, "E20.57.9", {"start": v(19.54, 60.29) * mm, "mid": v(19.61, 60.4) * mm, "end": v(19.67, 60.52) * mm});
            skLineSegment(sketch, "E20.57.10", {"start": v(19.67, 60.52) * mm, "end": v(20.07, 61.66) * mm});
            skArc(sketch, "E20.57.11", {"start": v(21.07, 62.14) * mm, "mid": v(20.47, 62.1) * mm, "end": v(20.07, 61.66) * mm});
            skArc(sketch, "E20.58.0", {"start": v(10.23, 63.95) * mm, "mid": v(10.11, 64.58) * mm, "end": v(9.57, 64.91) * mm});
            skLineSegment(sketch, "E20.58.1", {"start": v(10, 63.02) * mm, "end": v(10.23, 63.95) * mm});
            skArc(sketch, "E20.58.2", {"start": v(10, 63.02) * mm, "mid": v(9.98, 62.89) * mm, "end": v(9.98, 62.76) * mm});
            skArc(sketch, "E20.58.3", {"start": v(9.98, 62.76) * mm, "mid": v(10.08, 61.93) * mm, "end": v(10.22, 61.1) * mm});
            skArc(sketch, "E20.58.4", {"start": v(10.22, 61.1) * mm, "mid": v(10.42, 60.71) * mm, "end": v(10.8, 60.49) * mm});
            skLineSegment(sketch, "E20.58.5", {"start": v(10.8, 60.49) * mm, "end": v(11.09, 60.42) * mm});
            skLineSegment(sketch, "E20.58.6", {"start": v(11.38, 60.35) * mm, "end": v(11.09, 60.42) * mm});
            skArc(sketch, "E20.58.7", {"start": v(11.38, 60.35) * mm, "mid": v(11.82, 60.38) * mm, "end": v(12.17, 60.64) * mm});
            skArc(sketch, "E20.58.8", {"start": v(13.13, 62) * mm, "mid": v(12.67, 61.3) * mm, "end": v(12.17, 60.64) * mm});
            skArc(sketch, "E20.58.9", {"start": v(13.13, 62) * mm, "mid": v(13.2, 62.12) * mm, "end": v(13.23, 62.24) * mm});
            skLineSegment(sketch, "E20.58.10", {"start": v(13.23, 62.24) * mm, "end": v(13.52, 63.42) * mm});
            skArc(sketch, "E20.58.11", {"start": v(14.46, 64) * mm, "mid": v(13.87, 63.9) * mm, "end": v(13.52, 63.42) * mm});
            skArc(sketch, "E20.59.0", {"start": v(3.48, 64.67) * mm, "mid": v(3.3, 65.28) * mm, "end": v(2.74, 65.56) * mm});
            skLineSegment(sketch, "E20.59.1", {"start": v(3.36, 63.72) * mm, "end": v(3.48, 64.67) * mm});
            skArc(sketch, "E20.59.2", {"start": v(3.36, 63.72) * mm, "mid": v(3.35, 63.59) * mm, "end": v(3.37, 63.46) * mm});
            skArc(sketch, "E20.59.3", {"start": v(3.37, 63.46) * mm, "mid": v(3.55, 62.64) * mm, "end": v(3.77, 61.84) * mm});
            skArc(sketch, "E20.59.4", {"start": v(3.77, 61.84) * mm, "mid": v(4.01, 61.47) * mm, "end": v(4.42, 61.29) * mm});
            skLineSegment(sketch, "E20.59.5", {"start": v(4.42, 61.29) * mm, "end": v(4.7, 61.24) * mm});
            skLineSegment(sketch, "E20.59.6", {"start": v(5, 61.2) * mm, "end": v(4.7, 61.24) * mm});
            skArc(sketch, "E20.59.7", {"start": v(5, 61.2) * mm, "mid": v(5.44, 61.28) * mm, "end": v(5.77, 61.58) * mm});
            skArc(sketch, "E20.59.8", {"start": v(6.58, 63.03) * mm, "mid": v(6.19, 62.3) * mm, "end": v(5.77, 61.58) * mm});
            skArc(sketch, "E20.59.9", {"start": v(6.58, 63.03) * mm, "mid": v(6.63, 63.15) * mm, "end": v(6.65, 63.28) * mm});
            skLineSegment(sketch, "E20.59.10", {"start": v(6.65, 63.28) * mm, "end": v(6.81, 64.49) * mm});
            skArc(sketch, "E20.59.11", {"start": v(7.69, 65.16) * mm, "mid": v(7.11, 65) * mm, "end": v(6.81, 64.49) * mm});
            skArc(sketch, "E21.trimOffspring", {"start": v(-10.95, 64.7) * mm, "mid": v(-11.9, 64.53) * mm, "end": v(-12.83, 64.35) * mm});
            skArc(sketch, "E22.trimOffspring", {"start": v(-24.17, 61) * mm, "mid": v(-25.05, 60.65) * mm, "end": v(-25.93, 60.28) * mm});
            skArc(sketch, "E23.trimOffspring", {"start": v(-30.4, 58.14) * mm, "mid": v(-31.25, 57.7) * mm, "end": v(-32.08, 57.24) * mm});
            skArc(sketch, "E24.trimOffspring", {"start": v(-36.32, 54.65) * mm, "mid": v(-37.11, 54.11) * mm, "end": v(-37.9, 53.57) * mm});
            skArc(sketch, "E25.trimOffspring", {"start": v(-41.83, 50.55) * mm, "mid": v(-42.56, 49.94) * mm, "end": v(-43.28, 49.32) * mm});
            skArc(sketch, "E26.trimOffspring", {"start": v(-51.43, 40.75) * mm, "mid": v(-52.02, 40) * mm, "end": v(-52.6, 39.24) * mm});
            skArc(sketch, "E27.trimOffspring", {"start": v(-61.5, 22.86) * mm, "mid": v(-61.83, 21.97) * mm, "end": v(-62.14, 21.07) * mm});
            skArc(sketch, "E28.trimOffspring", {"start": v(-55.4, 35.15) * mm, "mid": v(-55.91, 34.34) * mm, "end": v(-56.4, 33.53) * mm});
            skArc(sketch, "E29.trimOffspring", {"start": v(-58.78, 29.17) * mm, "mid": v(-59.2, 28.3) * mm, "end": v(-59.6, 27.45) * mm});
            skArc(sketch, "E30.trimOffspring", {"start": v(-64.91, 9.57) * mm, "mid": v(-65.05, 8.63) * mm, "end": v(-65.16, 7.69) * mm});
            skArc(sketch, "E31.trimOffspring", {"start": v(-63.56, 16.3) * mm, "mid": v(-63.79, 15.38) * mm, "end": v(-64, 14.46) * mm});
            skArc(sketch, "E32.trimOffspring", {"start": v(-65.56, 2.74) * mm, "mid": v(-65.6, 1.78) * mm, "end": v(-65.61, 0.83) * mm});
            skArc(sketch, "E33.trimOffspring", {"start": v(-65.49, -4.13) * mm, "mid": v(-65.42, -5.08) * mm, "end": v(-65.34, -6.03) * mm});
            skArc(sketch, "E34.trimOffspring", {"start": v(-64.7, -10.95) * mm, "mid": v(-64.53, -11.9) * mm, "end": v(-64.35, -12.83) * mm});
            skArc(sketch, "E35.trimOffspring", {"start": v(-63.2, -17.66) * mm, "mid": v(-62.93, -18.57) * mm, "end": v(-62.66, -19.48) * mm});
            skArc(sketch, "E36.trimOffspring", {"start": v(-61, -24.17) * mm, "mid": v(-60.65, -25.05) * mm, "end": v(-60.28, -25.93) * mm});
            skArc(sketch, "E37.trimOffspring", {"start": v(-58.14, -30.4) * mm, "mid": v(-57.7, -31.25) * mm, "end": v(-57.24, -32.08) * mm});
            skArc(sketch, "E38.trimOffspring", {"start": v(-54.65, -36.32) * mm, "mid": v(-54.11, -37.11) * mm, "end": v(-53.57, -37.9) * mm});
            skArc(sketch, "E39.trimOffspring", {"start": v(-50.55, -41.83) * mm, "mid": v(-49.94, -42.56) * mm, "end": v(-49.32, -43.28) * mm});
            skArc(sketch, "E40.trimOffspring", {"start": v(-45.9, -46.89) * mm, "mid": v(-45.22, -47.55) * mm, "end": v(-44.52, -48.2) * mm});
            skArc(sketch, "E41.trimOffspring", {"start": v(-40.75, -51.43) * mm, "mid": v(-40, -52.02) * mm, "end": v(-39.24, -52.6) * mm});
            skArc(sketch, "E42.trimOffspring", {"start": v(-35.15, -55.4) * mm, "mid": v(-34.34, -55.91) * mm, "end": v(-33.53, -56.4) * mm});
            skArc(sketch, "E43.trimOffspring", {"start": v(-29.17, -58.78) * mm, "mid": v(-28.3, -59.2) * mm, "end": v(-27.45, -59.6) * mm});
            skArc(sketch, "E44.trimOffspring", {"start": v(-22.86, -61.5) * mm, "mid": v(-21.97, -61.83) * mm, "end": v(-21.07, -62.14) * mm});
            skArc(sketch, "E45.trimOffspring", {"start": v(-16.3, -63.56) * mm, "mid": v(-15.38, -63.79) * mm, "end": v(-14.46, -64) * mm});
            skArc(sketch, "E46.trimOffspring", {"start": v(-9.57, -64.91) * mm, "mid": v(-8.63, -65.05) * mm, "end": v(-7.69, -65.16) * mm});
            skArc(sketch, "E47.trimOffspring", {"start": v(-2.74, -65.56) * mm, "mid": v(-1.78, -65.6) * mm, "end": v(-0.83, -65.61) * mm});
            skArc(sketch, "E48.trimOffspring", {"start": v(4.13, -65.49) * mm, "mid": v(5.08, -65.42) * mm, "end": v(6.03, -65.34) * mm});
            skArc(sketch, "E49.trimOffspring", {"start": v(10.95, -64.7) * mm, "mid": v(11.9, -64.53) * mm, "end": v(12.83, -64.35) * mm});
            skArc(sketch, "E50.trimOffspring", {"start": v(17.66, -63.2) * mm, "mid": v(18.57, -62.93) * mm, "end": v(19.48, -62.66) * mm});
            skArc(sketch, "E51.trimOffspring", {"start": v(24.17, -61) * mm, "mid": v(25.05, -60.65) * mm, "end": v(25.93, -60.28) * mm});
            skArc(sketch, "E52.trimOffspring", {"start": v(30.4, -58.14) * mm, "mid": v(31.25, -57.7) * mm, "end": v(32.08, -57.24) * mm});
            skArc(sketch, "E53.trimOffspring", {"start": v(36.32, -54.65) * mm, "mid": v(37.11, -54.11) * mm, "end": v(37.9, -53.57) * mm});
            skArc(sketch, "E54.trimOffspring", {"start": v(41.83, -50.55) * mm, "mid": v(42.56, -49.94) * mm, "end": v(43.28, -49.32) * mm});
            skArc(sketch, "E55.trimOffspring", {"start": v(46.89, -45.9) * mm, "mid": v(47.55, -45.22) * mm, "end": v(48.2, -44.52) * mm});
            skArc(sketch, "E56.trimOffspring", {"start": v(51.43, -40.75) * mm, "mid": v(52.02, -40) * mm, "end": v(52.6, -39.24) * mm});
            skArc(sketch, "E57.trimOffspring", {"start": v(55.4, -35.15) * mm, "mid": v(55.91, -34.34) * mm, "end": v(56.4, -33.53) * mm});
            skArc(sketch, "E58.trimOffspring", {"start": v(58.78, -29.17) * mm, "mid": v(59.2, -28.3) * mm, "end": v(59.6, -27.45) * mm});
            skArc(sketch, "E59.trimOffspring", {"start": v(61.5, -22.86) * mm, "mid": v(61.83, -21.97) * mm, "end": v(62.14, -21.07) * mm});
            skArc(sketch, "E60.trimOffspring", {"start": v(63.56, -16.3) * mm, "mid": v(63.79, -15.38) * mm, "end": v(64, -14.46) * mm});
            skArc(sketch, "E61.trimOffspring", {"start": v(64.91, -9.57) * mm, "mid": v(65.05, -8.63) * mm, "end": v(65.16, -7.69) * mm});
            skArc(sketch, "E62.trimOffspring", {"start": v(65.56, -2.74) * mm, "mid": v(65.6, -1.78) * mm, "end": v(65.61, -0.83) * mm});
            skArc(sketch, "E63.trimOffspring", {"start": v(65.49, 4.13) * mm, "mid": v(65.42, 5.08) * mm, "end": v(65.34, 6.03) * mm});
            skArc(sketch, "E64.trimOffspring", {"start": v(64.7, 10.95) * mm, "mid": v(64.53, 11.9) * mm, "end": v(64.35, 12.83) * mm});
            skArc(sketch, "E65.trimOffspring", {"start": v(63.2, 17.66) * mm, "mid": v(62.93, 18.57) * mm, "end": v(62.66, 19.48) * mm});
            skArc(sketch, "E66.trimOffspring", {"start": v(61, 24.17) * mm, "mid": v(60.65, 25.05) * mm, "end": v(60.28, 25.93) * mm});
            skArc(sketch, "E67.trimOffspring", {"start": v(58.14, 30.4) * mm, "mid": v(57.7, 31.25) * mm, "end": v(57.24, 32.08) * mm});
            skArc(sketch, "E68.trimOffspring", {"start": v(54.65, 36.32) * mm, "mid": v(54.11, 37.11) * mm, "end": v(53.57, 37.9) * mm});
            skArc(sketch, "E69.trimOffspring", {"start": v(50.55, 41.83) * mm, "mid": v(49.94, 42.56) * mm, "end": v(49.32, 43.28) * mm});
            skArc(sketch, "E70.trimOffspring", {"start": v(45.9, 46.89) * mm, "mid": v(45.22, 47.55) * mm, "end": v(44.52, 48.2) * mm});
            skArc(sketch, "E71.trimOffspring", {"start": v(40.75, 51.43) * mm, "mid": v(40, 52.02) * mm, "end": v(39.24, 52.6) * mm});
            skArc(sketch, "E72.trimOffspring", {"start": v(35.15, 55.4) * mm, "mid": v(34.34, 55.91) * mm, "end": v(33.53, 56.4) * mm});
            skArc(sketch, "E73.trimOffspring", {"start": v(29.17, 58.78) * mm, "mid": v(28.3, 59.2) * mm, "end": v(27.45, 59.6) * mm});
            skArc(sketch, "E74.trimOffspring", {"start": v(22.86, 61.5) * mm, "mid": v(21.97, 61.83) * mm, "end": v(21.07, 62.14) * mm});
            skArc(sketch, "E75.trimOffspring", {"start": v(16.3, 63.56) * mm, "mid": v(15.38, 63.79) * mm, "end": v(14.46, 64) * mm});
            skArc(sketch, "E76.trimOffspring", {"start": v(9.57, 64.91) * mm, "mid": v(8.63, 65.05) * mm, "end": v(7.69, 65.16) * mm});
            skArc(sketch, "E77.trimOffspring", {"start": v(2.74, 65.56) * mm, "mid": v(1.78, 65.6) * mm, "end": v(0.83, 65.61) * mm});
            skCircle(sketch, "E78", {"center": v(0, 0) * mm, "radius": 76.37 * mm});
            skLineSegment(sketch, "E79", {"start": v(-48.2, 44.52) * mm, "end": v(-46.89, 45.9) * mm});
            skLineSegment(sketch, "E80", {"start": v(-19.48, 62.66) * mm, "end": v(-17.66, 63.2) * mm});
            skSolve(sketch);
        }
        {
            var Q0;
            Q0 = qSketchRegion(id + "F0", true);
            extrude(context, id + "F1", {"entities" : qUnion([Q0]), "depth" : 25.4 * mm});
        }
        {
            var Q0;
            Q0=makeQuery(id+"F1.opExtrude","CAP_FACE",FACE,{"disambiguationData":[OSD([sQuery(id+"F0.wireOp",EDGE,"E0"),sQuery(id+"F0.wireOp",EDGE,"E3.MirrorCS"),sQuery(id+"F0.wireOp",EDGE,"E4.MirrorCS"),sQuery(id+"F0.wireOp",EDGE,"E5.MirrorCS"),sQuery(id+"F0.wireOp",EDGE,"E6.MirrorCS"),sQuery(id+"F0.wireOp",EDGE,"E7.MirrorCS"),sQuery(id+"F0.wireOp",EDGE,"E8.MirrorCS"),sQuery(id+"F0.wireOp",EDGE,"E14.filletArc"),sQuery(id+"F0.wireOp",EDGE,"E15.filletArc"),sQuery(id+"F0.wireOp",EDGE,"E16.filletArc"),sQuery(id+"F0.wireOp",EDGE,"E17.filletArc"),sQuery(id+"F0.wireOp",EDGE,"E18.filletArc"),sQuery(id+"F0.wireOp",EDGE,"E19.filletArc"),sQuery(id+"F0.wireOp",EDGE,"E20.1.0"),sQuery(id+"F0.wireOp",EDGE,"E20.1.1"),sQuery(id+"F0.wireOp",EDGE,"E20.1.2"),sQuery(id+"F0.wireOp",EDGE,"E20.1.3"),sQuery(id+"F0.wireOp",EDGE,"E20.1.4"),sQuery(id+"F0.wireOp",EDGE,"E20.1.5"),sQuery(id+"F0.wireOp",EDGE,"E20.1.6"),sQuery(id+"F0.wireOp",EDGE,"E20.1.7"),sQuery(id+"F0.wireOp",EDGE,"E20.1.8"),sQuery(id+"F0.wireOp",EDGE,"E20.1.9"),sQuery(id+"F0.wireOp",EDGE,"E20.1.10"),sQuery(id+"F0.wireOp",EDGE,"E20.1.11"),sQuery(id+"F0.wireOp",EDGE,"E20.2.0"),sQuery(id+"F0.wireOp",EDGE,"E20.2.1"),sQuery(id+"F0.wireOp",EDGE,"E20.2.2"),sQuery(id+"F0.wireOp",EDGE,"E20.2.3"),sQuery(id+"F0.wireOp",EDGE,"E20.2.4"),sQuery(id+"F0.wireOp",EDGE,"E20.2.5"),sQuery(id+"F0.wireOp",EDGE,"E20.2.6"),sQuery(id+"F0.wireOp",EDGE,"E20.2.7"),sQuery(id+"F0.wireOp",EDGE,"E20.2.8"),sQuery(id+"F0.wireOp",EDGE,"E20.2.9"),sQuery(id+"F0.wireOp",EDGE,"E20.2.10"),sQuery(id+"F0.wireOp",EDGE,"E20.2.11"),sQuery(id+"F0.wireOp",EDGE,"E20.3.0"),sQuery(id+"F0.wireOp",EDGE,"E20.3.1"),sQuery(id+"F0.wireOp",EDGE,"E20.3.2"),sQuery(id+"F0.wireOp",EDGE,"E20.3.3"),sQuery(id+"F0.wireOp",EDGE,"E20.3.4"),sQuery(id+"F0.wireOp",EDGE,"E20.3.5"),sQuery(id+"F0.wireOp",EDGE,"E20.3.6"),sQuery(id+"F0.wireOp",EDGE,"E20.3.7"),sQuery(id+"F0.wireOp",EDGE,"E20.3.8"),sQuery(id+"F0.wireOp",EDGE,"E20.3.9"),sQuery(id+"F0.wireOp",EDGE,"E20.3.10"),sQuery(id+"F0.wireOp",EDGE,"E20.3.11"),sQuery(id+"F0.wireOp",EDGE,"E20.4.0"),sQuery(id+"F0.wireOp",EDGE,"E20.4.1"),sQuery(id+"F0.wireOp",EDGE,"E20.4.2"),sQuery(id+"F0.wireOp",EDGE,"E20.4.3"),sQuery(id+"F0.wireOp",EDGE,"E20.4.4"),sQuery(id+"F0.wireOp",EDGE,"E20.4.5"),sQuery(id+"F0.wireOp",EDGE,"E20.4.6"),sQuery(id+"F0.wireOp",EDGE,"E20.4.7"),sQuery(id+"F0.wireOp",EDGE,"E20.4.8"),sQuery(id+"F0.wireOp",EDGE,"E20.4.9"),sQuery(id+"F0.wireOp",EDGE,"E20.4.10"),sQuery(id+"F0.wireOp",EDGE,"E20.4.11"),sQuery(id+"F0.wireOp",EDGE,"E20.5.0"),sQuery(id+"F0.wireOp",EDGE,"E20.5.1"),sQuery(id+"F0.wireOp",EDGE,"E20.5.2"),sQuery(id+"F0.wireOp",EDGE,"E20.5.3"),sQuery(id+"F0.wireOp",EDGE,"E20.5.4"),sQuery(id+"F0.wireOp",EDGE,"E20.5.5"),sQuery(id+"F0.wireOp",EDGE,"E20.5.6"),sQuery(id+"F0.wireOp",EDGE,"E20.5.7"),sQuery(id+"F0.wireOp",EDGE,"E20.5.8"),sQuery(id+"F0.wireOp",EDGE,"E20.5.9"),sQuery(id+"F0.wireOp",EDGE,"E20.5.10"),sQuery(id+"F0.wireOp",EDGE,"E20.5.11"),sQuery(id+"F0.wireOp",EDGE,"E20.6.0"),sQuery(id+"F0.wireOp",EDGE,"E20.6.1"),sQuery(id+"F0.wireOp",EDGE,"E20.6.2"),sQuery(id+"F0.wireOp",EDGE,"E20.6.3"),sQuery(id+"F0.wireOp",EDGE,"E20.6.4"),sQuery(id+"F0.wireOp",EDGE,"E20.6.5"),sQuery(id+"F0.wireOp",EDGE,"E20.6.6"),sQuery(id+"F0.wireOp",EDGE,"E20.6.7"),sQuery(id+"F0.wireOp",EDGE,"E20.6.8"),sQuery(id+"F0.wireOp",EDGE,"E20.6.9"),sQuery(id+"F0.wireOp",EDGE,"E20.6.10"),sQuery(id+"F0.wireOp",EDGE,"E20.6.11"),sQuery(id+"F0.wireOp",EDGE,"E20.7.0"),sQuery(id+"F0.wireOp",EDGE,"E20.7.1"),sQuery(id+"F0.wireOp",EDGE,"E20.7.2"),sQuery(id+"F0.wireOp",EDGE,"E20.7.3"),sQuery(id+"F0.wireOp",EDGE,"E20.7.4"),sQuery(id+"F0.wireOp",EDGE,"E20.7.5"),sQuery(id+"F0.wireOp",EDGE,"E20.7.6"),sQuery(id+"F0.wireOp",EDGE,"E20.7.7"),sQuery(id+"F0.wireOp",EDGE,"E20.7.8"),sQuery(id+"F0.wireOp",EDGE,"E20.7.9"),sQuery(id+"F0.wireOp",EDGE,"E20.7.10"),sQuery(id+"F0.wireOp",EDGE,"E20.7.11"),sQuery(id+"F0.wireOp",EDGE,"E20.8.0"),sQuery(id+"F0.wireOp",EDGE,"E20.8.1"),sQuery(id+"F0.wireOp",EDGE,"E20.8.2"),sQuery(id+"F0.wireOp",EDGE,"E20.8.3"),sQuery(id+"F0.wireOp",EDGE,"E20.8.4"),sQuery(id+"F0.wireOp",EDGE,"E20.8.5"),sQuery(id+"F0.wireOp",EDGE,"E20.8.6"),sQuery(id+"F0.wireOp",EDGE,"E20.8.7"),sQuery(id+"F0.wireOp",EDGE,"E20.8.8"),sQuery(id+"F0.wireOp",EDGE,"E20.8.9"),sQuery(id+"F0.wireOp",EDGE,"E20.8.10"),sQuery(id+"F0.wireOp",EDGE,"E20.8.11"),sQuery(id+"F0.wireOp",EDGE,"E20.9.0"),sQuery(id+"F0.wireOp",EDGE,"E20.9.1"),sQuery(id+"F0.wireOp",EDGE,"E20.9.2"),sQuery(id+"F0.wireOp",EDGE,"E20.9.3"),sQuery(id+"F0.wireOp",EDGE,"E20.9.4"),sQuery(id+"F0.wireOp",EDGE,"E20.9.5"),sQuery(id+"F0.wireOp",EDGE,"E20.9.6"),sQuery(id+"F0.wireOp",EDGE,"E20.9.7"),sQuery(id+"F0.wireOp",EDGE,"E20.9.8"),sQuery(id+"F0.wireOp",EDGE,"E20.9.9"),sQuery(id+"F0.wireOp",EDGE,"E20.9.10"),sQuery(id+"F0.wireOp",EDGE,"E20.9.11"),sQuery(id+"F0.wireOp",EDGE,"E20.10.0"),sQuery(id+"F0.wireOp",EDGE,"E20.10.1"),sQuery(id+"F0.wireOp",EDGE,"E20.10.2"),sQuery(id+"F0.wireOp",EDGE,"E20.10.3"),sQuery(id+"F0.wireOp",EDGE,"E20.10.4"),sQuery(id+"F0.wireOp",EDGE,"E20.10.5"),sQuery(id+"F0.wireOp",EDGE,"E20.10.6"),sQuery(id+"F0.wireOp",EDGE,"E20.10.7"),sQuery(id+"F0.wireOp",EDGE,"E20.10.8"),sQuery(id+"F0.wireOp",EDGE,"E20.10.9"),sQuery(id+"F0.wireOp",EDGE,"E20.10.10"),sQuery(id+"F0.wireOp",EDGE,"E20.10.11"),sQuery(id+"F0.wireOp",EDGE,"E20.11.0"),sQuery(id+"F0.wireOp",EDGE,"E20.11.1"),sQuery(id+"F0.wireOp",EDGE,"E20.11.2"),sQuery(id+"F0.wireOp",EDGE,"E20.11.3"),sQuery(id+"F0.wireOp",EDGE,"E20.11.4"),sQuery(id+"F0.wireOp",EDGE,"E20.11.5"),sQuery(id+"F0.wireOp",EDGE,"E20.11.6"),sQuery(id+"F0.wireOp",EDGE,"E20.11.7"),sQuery(id+"F0.wireOp",EDGE,"E20.11.8"),sQuery(id+"F0.wireOp",EDGE,"E20.11.9"),sQuery(id+"F0.wireOp",EDGE,"E20.11.10"),sQuery(id+"F0.wireOp",EDGE,"E20.11.11"),sQuery(id+"F0.wireOp",EDGE,"E20.12.0"),sQuery(id+"F0.wireOp",EDGE,"E20.12.1"),sQuery(id+"F0.wireOp",EDGE,"E20.12.2"),sQuery(id+"F0.wireOp",EDGE,"E20.12.3"),sQuery(id+"F0.wireOp",EDGE,"E20.12.4"),sQuery(id+"F0.wireOp",EDGE,"E20.12.5"),sQuery(id+"F0.wireOp",EDGE,"E20.12.6"),sQuery(id+"F0.wireOp",EDGE,"E20.12.7"),sQuery(id+"F0.wireOp",EDGE,"E20.12.8"),sQuery(id+"F0.wireOp",EDGE,"E20.12.9"),sQuery(id+"F0.wireOp",EDGE,"E20.12.10"),sQuery(id+"F0.wireOp",EDGE,"E20.12.11"),sQuery(id+"F0.wireOp",EDGE,"E20.13.0"),sQuery(id+"F0.wireOp",EDGE,"E20.13.1"),sQuery(id+"F0.wireOp",EDGE,"E20.13.2"),sQuery(id+"F0.wireOp",EDGE,"E20.13.3"),sQuery(id+"F0.wireOp",EDGE,"E20.13.4"),sQuery(id+"F0.wireOp",EDGE,"E20.13.5"),sQuery(id+"F0.wireOp",EDGE,"E20.13.6"),sQuery(id+"F0.wireOp",EDGE,"E20.13.7"),sQuery(id+"F0.wireOp",EDGE,"E20.13.8"),sQuery(id+"F0.wireOp",EDGE,"E20.13.9"),sQuery(id+"F0.wireOp",EDGE,"E20.13.10"),sQuery(id+"F0.wireOp",EDGE,"E20.13.11"),sQuery(id+"F0.wireOp",EDGE,"E20.14.0"),sQuery(id+"F0.wireOp",EDGE,"E20.14.1"),sQuery(id+"F0.wireOp",EDGE,"E20.14.2"),sQuery(id+"F0.wireOp",EDGE,"E20.14.3"),sQuery(id+"F0.wireOp",EDGE,"E20.14.4"),sQuery(id+"F0.wireOp",EDGE,"E20.14.5"),sQuery(id+"F0.wireOp",EDGE,"E20.14.6"),sQuery(id+"F0.wireOp",EDGE,"E20.14.7"),sQuery(id+"F0.wireOp",EDGE,"E20.14.8"),sQuery(id+"F0.wireOp",EDGE,"E20.14.9"),sQuery(id+"F0.wireOp",EDGE,"E20.14.10"),sQuery(id+"F0.wireOp",EDGE,"E20.14.11"),sQuery(id+"F0.wireOp",EDGE,"E20.15.0"),sQuery(id+"F0.wireOp",EDGE,"E20.15.1"),sQuery(id+"F0.wireOp",EDGE,"E20.15.2"),sQuery(id+"F0.wireOp",EDGE,"E20.15.3"),sQuery(id+"F0.wireOp",EDGE,"E20.15.4"),sQuery(id+"F0.wireOp",EDGE,"E20.15.5"),sQuery(id+"F0.wireOp",EDGE,"E20.15.6"),sQuery(id+"F0.wireOp",EDGE,"E20.15.7"),sQuery(id+"F0.wireOp",EDGE,"E20.15.8"),sQuery(id+"F0.wireOp",EDGE,"E20.15.9"),sQuery(id+"F0.wireOp",EDGE,"E20.15.10"),sQuery(id+"F0.wireOp",EDGE,"E20.15.11"),sQuery(id+"F0.wireOp",EDGE,"E20.16.0"),sQuery(id+"F0.wireOp",EDGE,"E20.16.1"),sQuery(id+"F0.wireOp",EDGE,"E20.16.2"),sQuery(id+"F0.wireOp",EDGE,"E20.16.3"),sQuery(id+"F0.wireOp",EDGE,"E20.16.4"),sQuery(id+"F0.wireOp",EDGE,"E20.16.5"),sQuery(id+"F0.wireOp",EDGE,"E20.16.6"),sQuery(id+"F0.wireOp",EDGE,"E20.16.7"),sQuery(id+"F0.wireOp",EDGE,"E20.16.8"),sQuery(id+"F0.wireOp",EDGE,"E20.16.9"),sQuery(id+"F0.wireOp",EDGE,"E20.16.10"),sQuery(id+"F0.wireOp",EDGE,"E20.16.11"),sQuery(id+"F0.wireOp",EDGE,"E20.17.0"),sQuery(id+"F0.wireOp",EDGE,"E20.17.1"),sQuery(id+"F0.wireOp",EDGE,"E20.17.2"),sQuery(id+"F0.wireOp",EDGE,"E20.17.3"),sQuery(id+"F0.wireOp",EDGE,"E20.17.4"),sQuery(id+"F0.wireOp",EDGE,"E20.17.5"),sQuery(id+"F0.wireOp",EDGE,"E20.17.6"),sQuery(id+"F0.wireOp",EDGE,"E20.17.7"),sQuery(id+"F0.wireOp",EDGE,"E20.17.8"),sQuery(id+"F0.wireOp",EDGE,"E20.17.9"),sQuery(id+"F0.wireOp",EDGE,"E20.17.10"),sQuery(id+"F0.wireOp",EDGE,"E20.17.11"),sQuery(id+"F0.wireOp",EDGE,"E20.18.0"),sQuery(id+"F0.wireOp",EDGE,"E20.18.1"),sQuery(id+"F0.wireOp",EDGE,"E20.18.2"),sQuery(id+"F0.wireOp",EDGE,"E20.18.3"),sQuery(id+"F0.wireOp",EDGE,"E20.18.4"),sQuery(id+"F0.wireOp",EDGE,"E20.18.5"),sQuery(id+"F0.wireOp",EDGE,"E20.18.6"),sQuery(id+"F0.wireOp",EDGE,"E20.18.7"),sQuery(id+"F0.wireOp",EDGE,"E20.18.8"),sQuery(id+"F0.wireOp",EDGE,"E20.18.9"),sQuery(id+"F0.wireOp",EDGE,"E20.18.10"),sQuery(id+"F0.wireOp",EDGE,"E20.18.11"),sQuery(id+"F0.wireOp",EDGE,"E20.19.0"),sQuery(id+"F0.wireOp",EDGE,"E20.19.1"),sQuery(id+"F0.wireOp",EDGE,"E20.19.2"),sQuery(id+"F0.wireOp",EDGE,"E20.19.3"),sQuery(id+"F0.wireOp",EDGE,"E20.19.4"),sQuery(id+"F0.wireOp",EDGE,"E20.19.5"),sQuery(id+"F0.wireOp",EDGE,"E20.19.6"),sQuery(id+"F0.wireOp",EDGE,"E20.19.7"),sQuery(id+"F0.wireOp",EDGE,"E20.19.8"),sQuery(id+"F0.wireOp",EDGE,"E20.19.9"),sQuery(id+"F0.wireOp",EDGE,"E20.19.10"),sQuery(id+"F0.wireOp",EDGE,"E20.19.11"),sQuery(id+"F0.wireOp",EDGE,"E20.20.0"),sQuery(id+"F0.wireOp",EDGE,"E20.20.1"),sQuery(id+"F0.wireOp",EDGE,"E20.20.2"),sQuery(id+"F0.wireOp",EDGE,"E20.20.3"),sQuery(id+"F0.wireOp",EDGE,"E20.20.4"),sQuery(id+"F0.wireOp",EDGE,"E20.20.5"),sQuery(id+"F0.wireOp",EDGE,"E20.20.6"),sQuery(id+"F0.wireOp",EDGE,"E20.20.7"),sQuery(id+"F0.wireOp",EDGE,"E20.20.8"),sQuery(id+"F0.wireOp",EDGE,"E20.20.9"),sQuery(id+"F0.wireOp",EDGE,"E20.20.10"),sQuery(id+"F0.wireOp",EDGE,"E20.20.11"),sQuery(id+"F0.wireOp",EDGE,"E20.21.0"),sQuery(id+"F0.wireOp",EDGE,"E20.21.1"),sQuery(id+"F0.wireOp",EDGE,"E20.21.2"),sQuery(id+"F0.wireOp",EDGE,"E20.21.3"),sQuery(id+"F0.wireOp",EDGE,"E20.21.4"),sQuery(id+"F0.wireOp",EDGE,"E20.21.5"),sQuery(id+"F0.wireOp",EDGE,"E20.21.6"),sQuery(id+"F0.wireOp",EDGE,"E20.21.7"),sQuery(id+"F0.wireOp",EDGE,"E20.21.8"),sQuery(id+"F0.wireOp",EDGE,"E20.21.9"),sQuery(id+"F0.wireOp",EDGE,"E20.21.10"),sQuery(id+"F0.wireOp",EDGE,"E20.21.11"),sQuery(id+"F0.wireOp",EDGE,"E20.22.0"),sQuery(id+"F0.wireOp",EDGE,"E20.22.1"),sQuery(id+"F0.wireOp",EDGE,"E20.22.2"),sQuery(id+"F0.wireOp",EDGE,"E20.22.3"),sQuery(id+"F0.wireOp",EDGE,"E20.22.4"),sQuery(id+"F0.wireOp",EDGE,"E20.22.5"),sQuery(id+"F0.wireOp",EDGE,"E20.22.6"),sQuery(id+"F0.wireOp",EDGE,"E20.22.7"),sQuery(id+"F0.wireOp",EDGE,"E20.22.8"),sQuery(id+"F0.wireOp",EDGE,"E20.22.9"),sQuery(id+"F0.wireOp",EDGE,"E20.22.10"),sQuery(id+"F0.wireOp",EDGE,"E20.22.11"),sQuery(id+"F0.wireOp",EDGE,"E20.23.0"),sQuery(id+"F0.wireOp",EDGE,"E20.23.1"),sQuery(id+"F0.wireOp",EDGE,"E20.23.2"),sQuery(id+"F0.wireOp",EDGE,"E20.23.3"),sQuery(id+"F0.wireOp",EDGE,"E20.23.4"),sQuery(id+"F0.wireOp",EDGE,"E20.23.5"),sQuery(id+"F0.wireOp",EDGE,"E20.23.6"),sQuery(id+"F0.wireOp",EDGE,"E20.23.7"),sQuery(id+"F0.wireOp",EDGE,"E20.23.8"),sQuery(id+"F0.wireOp",EDGE,"E20.23.9"),sQuery(id+"F0.wireOp",EDGE,"E20.23.10"),sQuery(id+"F0.wireOp",EDGE,"E20.23.11"),sQuery(id+"F0.wireOp",EDGE,"E20.24.0"),sQuery(id+"F0.wireOp",EDGE,"E20.24.1"),sQuery(id+"F0.wireOp",EDGE,"E20.24.2"),sQuery(id+"F0.wireOp",EDGE,"E20.24.3"),sQuery(id+"F0.wireOp",EDGE,"E20.24.4"),sQuery(id+"F0.wireOp",EDGE,"E20.24.5"),sQuery(id+"F0.wireOp",EDGE,"E20.24.6"),sQuery(id+"F0.wireOp",EDGE,"E20.24.7"),sQuery(id+"F0.wireOp",EDGE,"E20.24.8"),sQuery(id+"F0.wireOp",EDGE,"E20.24.9"),sQuery(id+"F0.wireOp",EDGE,"E20.24.10"),sQuery(id+"F0.wireOp",EDGE,"E20.24.11"),sQuery(id+"F0.wireOp",EDGE,"E20.25.0"),sQuery(id+"F0.wireOp",EDGE,"E20.25.1"),sQuery(id+"F0.wireOp",EDGE,"E20.25.2"),sQuery(id+"F0.wireOp",EDGE,"E20.25.3"),sQuery(id+"F0.wireOp",EDGE,"E20.25.4"),sQuery(id+"F0.wireOp",EDGE,"E20.25.5"),sQuery(id+"F0.wireOp",EDGE,"E20.25.6"),sQuery(id+"F0.wireOp",EDGE,"E20.25.7"),sQuery(id+"F0.wireOp",EDGE,"E20.25.8"),sQuery(id+"F0.wireOp",EDGE,"E20.25.9"),sQuery(id+"F0.wireOp",EDGE,"E20.25.10"),sQuery(id+"F0.wireOp",EDGE,"E20.25.11"),sQuery(id+"F0.wireOp",EDGE,"E20.26.0"),sQuery(id+"F0.wireOp",EDGE,"E20.26.1"),sQuery(id+"F0.wireOp",EDGE,"E20.26.2"),sQuery(id+"F0.wireOp",EDGE,"E20.26.3"),sQuery(id+"F0.wireOp",EDGE,"E20.26.4"),sQuery(id+"F0.wireOp",EDGE,"E20.26.5"),sQuery(id+"F0.wireOp",EDGE,"E20.26.6"),sQuery(id+"F0.wireOp",EDGE,"E20.26.7"),sQuery(id+"F0.wireOp",EDGE,"E20.26.8"),sQuery(id+"F0.wireOp",EDGE,"E20.26.9"),sQuery(id+"F0.wireOp",EDGE,"E20.26.10"),sQuery(id+"F0.wireOp",EDGE,"E20.26.11"),sQuery(id+"F0.wireOp",EDGE,"E20.27.0"),sQuery(id+"F0.wireOp",EDGE,"E20.27.1"),sQuery(id+"F0.wireOp",EDGE,"E20.27.2"),sQuery(id+"F0.wireOp",EDGE,"E20.27.3"),sQuery(id+"F0.wireOp",EDGE,"E20.27.4"),sQuery(id+"F0.wireOp",EDGE,"E20.27.5"),sQuery(id+"F0.wireOp",EDGE,"E20.27.6"),sQuery(id+"F0.wireOp",EDGE,"E20.27.7"),sQuery(id+"F0.wireOp",EDGE,"E20.27.8"),sQuery(id+"F0.wireOp",EDGE,"E20.27.9"),sQuery(id+"F0.wireOp",EDGE,"E20.27.10"),sQuery(id+"F0.wireOp",EDGE,"E20.27.11"),sQuery(id+"F0.wireOp",EDGE,"E20.28.0"),sQuery(id+"F0.wireOp",EDGE,"E20.28.1"),sQuery(id+"F0.wireOp",EDGE,"E20.28.2"),sQuery(id+"F0.wireOp",EDGE,"E20.28.3"),sQuery(id+"F0.wireOp",EDGE,"E20.28.4"),sQuery(id+"F0.wireOp",EDGE,"E20.28.5"),sQuery(id+"F0.wireOp",EDGE,"E20.28.6"),sQuery(id+"F0.wireOp",EDGE,"E20.28.7"),sQuery(id+"F0.wireOp",EDGE,"E20.28.8"),sQuery(id+"F0.wireOp",EDGE,"E20.28.9"),sQuery(id+"F0.wireOp",EDGE,"E20.28.10"),sQuery(id+"F0.wireOp",EDGE,"E20.28.11"),sQuery(id+"F0.wireOp",EDGE,"E20.29.0"),sQuery(id+"F0.wireOp",EDGE,"E20.29.1"),sQuery(id+"F0.wireOp",EDGE,"E20.29.2"),sQuery(id+"F0.wireOp",EDGE,"E20.29.3"),sQuery(id+"F0.wireOp",EDGE,"E20.29.4"),sQuery(id+"F0.wireOp",EDGE,"E20.29.5"),sQuery(id+"F0.wireOp",EDGE,"E20.29.6"),sQuery(id+"F0.wireOp",EDGE,"E20.29.7"),sQuery(id+"F0.wireOp",EDGE,"E20.29.8"),sQuery(id+"F0.wireOp",EDGE,"E20.29.9"),sQuery(id+"F0.wireOp",EDGE,"E20.29.10"),sQuery(id+"F0.wireOp",EDGE,"E20.29.11"),sQuery(id+"F0.wireOp",EDGE,"E20.30.0"),sQuery(id+"F0.wireOp",EDGE,"E20.30.1"),sQuery(id+"F0.wireOp",EDGE,"E20.30.2"),sQuery(id+"F0.wireOp",EDGE,"E20.30.3"),sQuery(id+"F0.wireOp",EDGE,"E20.30.4"),sQuery(id+"F0.wireOp",EDGE,"E20.30.5"),sQuery(id+"F0.wireOp",EDGE,"E20.30.6"),sQuery(id+"F0.wireOp",EDGE,"E20.30.7"),sQuery(id+"F0.wireOp",EDGE,"E20.30.8"),sQuery(id+"F0.wireOp",EDGE,"E20.30.9"),sQuery(id+"F0.wireOp",EDGE,"E20.30.10"),sQuery(id+"F0.wireOp",EDGE,"E20.30.11"),sQuery(id+"F0.wireOp",EDGE,"E20.31.0"),sQuery(id+"F0.wireOp",EDGE,"E20.31.1"),sQuery(id+"F0.wireOp",EDGE,"E20.31.2"),sQuery(id+"F0.wireOp",EDGE,"E20.31.3"),sQuery(id+"F0.wireOp",EDGE,"E20.31.4"),sQuery(id+"F0.wireOp",EDGE,"E20.31.5"),sQuery(id+"F0.wireOp",EDGE,"E20.31.6"),sQuery(id+"F0.wireOp",EDGE,"E20.31.7"),sQuery(id+"F0.wireOp",EDGE,"E20.31.8"),sQuery(id+"F0.wireOp",EDGE,"E20.31.9"),sQuery(id+"F0.wireOp",EDGE,"E20.31.10"),sQuery(id+"F0.wireOp",EDGE,"E20.31.11"),sQuery(id+"F0.wireOp",EDGE,"E20.32.0"),sQuery(id+"F0.wireOp",EDGE,"E20.32.1"),sQuery(id+"F0.wireOp",EDGE,"E20.32.2"),sQuery(id+"F0.wireOp",EDGE,"E20.32.3"),sQuery(id+"F0.wireOp",EDGE,"E20.32.4"),sQuery(id+"F0.wireOp",EDGE,"E20.32.5"),sQuery(id+"F0.wireOp",EDGE,"E20.32.6"),sQuery(id+"F0.wireOp",EDGE,"E20.32.7"),sQuery(id+"F0.wireOp",EDGE,"E20.32.8"),sQuery(id+"F0.wireOp",EDGE,"E20.32.9"),sQuery(id+"F0.wireOp",EDGE,"E20.32.10"),sQuery(id+"F0.wireOp",EDGE,"E20.32.11"),sQuery(id+"F0.wireOp",EDGE,"E20.33.0"),sQuery(id+"F0.wireOp",EDGE,"E20.33.1"),sQuery(id+"F0.wireOp",EDGE,"E20.33.2"),sQuery(id+"F0.wireOp",EDGE,"E20.33.3"),sQuery(id+"F0.wireOp",EDGE,"E20.33.4"),sQuery(id+"F0.wireOp",EDGE,"E20.33.5"),sQuery(id+"F0.wireOp",EDGE,"E20.33.6"),sQuery(id+"F0.wireOp",EDGE,"E20.33.7"),sQuery(id+"F0.wireOp",EDGE,"E20.33.8"),sQuery(id+"F0.wireOp",EDGE,"E20.33.9"),sQuery(id+"F0.wireOp",EDGE,"E20.33.10"),sQuery(id+"F0.wireOp",EDGE,"E20.33.11"),sQuery(id+"F0.wireOp",EDGE,"E20.34.0"),sQuery(id+"F0.wireOp",EDGE,"E20.34.1"),sQuery(id+"F0.wireOp",EDGE,"E20.34.2"),sQuery(id+"F0.wireOp",EDGE,"E20.34.3"),sQuery(id+"F0.wireOp",EDGE,"E20.34.4"),sQuery(id+"F0.wireOp",EDGE,"E20.34.5"),sQuery(id+"F0.wireOp",EDGE,"E20.34.6"),sQuery(id+"F0.wireOp",EDGE,"E20.34.7"),sQuery(id+"F0.wireOp",EDGE,"E20.34.8"),sQuery(id+"F0.wireOp",EDGE,"E20.34.9"),sQuery(id+"F0.wireOp",EDGE,"E20.34.10"),sQuery(id+"F0.wireOp",EDGE,"E20.34.11"),sQuery(id+"F0.wireOp",EDGE,"E20.35.0"),sQuery(id+"F0.wireOp",EDGE,"E20.35.1"),sQuery(id+"F0.wireOp",EDGE,"E20.35.2"),sQuery(id+"F0.wireOp",EDGE,"E20.35.3"),sQuery(id+"F0.wireOp",EDGE,"E20.35.4"),sQuery(id+"F0.wireOp",EDGE,"E20.35.5"),sQuery(id+"F0.wireOp",EDGE,"E20.35.6"),sQuery(id+"F0.wireOp",EDGE,"E20.35.7"),sQuery(id+"F0.wireOp",EDGE,"E20.35.8"),sQuery(id+"F0.wireOp",EDGE,"E20.35.9"),sQuery(id+"F0.wireOp",EDGE,"E20.35.10"),sQuery(id+"F0.wireOp",EDGE,"E20.35.11"),sQuery(id+"F0.wireOp",EDGE,"E20.36.0"),sQuery(id+"F0.wireOp",EDGE,"E20.36.1"),sQuery(id+"F0.wireOp",EDGE,"E20.36.2"),sQuery(id+"F0.wireOp",EDGE,"E20.36.3"),sQuery(id+"F0.wireOp",EDGE,"E20.36.4"),sQuery(id+"F0.wireOp",EDGE,"E20.36.5"),sQuery(id+"F0.wireOp",EDGE,"E20.36.6"),sQuery(id+"F0.wireOp",EDGE,"E20.36.7"),sQuery(id+"F0.wireOp",EDGE,"E20.36.8"),sQuery(id+"F0.wireOp",EDGE,"E20.36.9"),sQuery(id+"F0.wireOp",EDGE,"E20.36.10"),sQuery(id+"F0.wireOp",EDGE,"E20.36.11"),sQuery(id+"F0.wireOp",EDGE,"E20.37.0"),sQuery(id+"F0.wireOp",EDGE,"E20.37.1"),sQuery(id+"F0.wireOp",EDGE,"E20.37.2"),sQuery(id+"F0.wireOp",EDGE,"E20.37.3"),sQuery(id+"F0.wireOp",EDGE,"E20.37.4"),sQuery(id+"F0.wireOp",EDGE,"E20.37.5"),sQuery(id+"F0.wireOp",EDGE,"E20.37.6"),sQuery(id+"F0.wireOp",EDGE,"E20.37.7"),sQuery(id+"F0.wireOp",EDGE,"E20.37.8"),sQuery(id+"F0.wireOp",EDGE,"E20.37.9"),sQuery(id+"F0.wireOp",EDGE,"E20.37.10"),sQuery(id+"F0.wireOp",EDGE,"E20.37.11"),sQuery(id+"F0.wireOp",EDGE,"E20.38.0"),sQuery(id+"F0.wireOp",EDGE,"E20.38.1"),sQuery(id+"F0.wireOp",EDGE,"E20.38.2"),sQuery(id+"F0.wireOp",EDGE,"E20.38.3"),sQuery(id+"F0.wireOp",EDGE,"E20.38.4"),sQuery(id+"F0.wireOp",EDGE,"E20.38.5"),sQuery(id+"F0.wireOp",EDGE,"E20.38.6"),sQuery(id+"F0.wireOp",EDGE,"E20.38.7"),sQuery(id+"F0.wireOp",EDGE,"E20.38.8"),sQuery(id+"F0.wireOp",EDGE,"E20.38.9"),sQuery(id+"F0.wireOp",EDGE,"E20.38.10"),sQuery(id+"F0.wireOp",EDGE,"E20.38.11"),sQuery(id+"F0.wireOp",EDGE,"E20.39.0"),sQuery(id+"F0.wireOp",EDGE,"E20.39.1"),sQuery(id+"F0.wireOp",EDGE,"E20.39.2"),sQuery(id+"F0.wireOp",EDGE,"E20.39.3"),sQuery(id+"F0.wireOp",EDGE,"E20.39.4"),sQuery(id+"F0.wireOp",EDGE,"E20.39.5"),sQuery(id+"F0.wireOp",EDGE,"E20.39.6"),sQuery(id+"F0.wireOp",EDGE,"E20.39.7"),sQuery(id+"F0.wireOp",EDGE,"E20.39.8"),sQuery(id+"F0.wireOp",EDGE,"E20.39.9"),sQuery(id+"F0.wireOp",EDGE,"E20.39.10"),sQuery(id+"F0.wireOp",EDGE,"E20.39.11"),sQuery(id+"F0.wireOp",EDGE,"E20.40.0"),sQuery(id+"F0.wireOp",EDGE,"E20.40.1"),sQuery(id+"F0.wireOp",EDGE,"E20.40.2"),sQuery(id+"F0.wireOp",EDGE,"E20.40.3"),sQuery(id+"F0.wireOp",EDGE,"E20.40.4"),sQuery(id+"F0.wireOp",EDGE,"E20.40.5"),sQuery(id+"F0.wireOp",EDGE,"E20.40.6"),sQuery(id+"F0.wireOp",EDGE,"E20.40.7"),sQuery(id+"F0.wireOp",EDGE,"E20.40.8"),sQuery(id+"F0.wireOp",EDGE,"E20.40.9"),sQuery(id+"F0.wireOp",EDGE,"E20.40.10"),sQuery(id+"F0.wireOp",EDGE,"E20.40.11"),sQuery(id+"F0.wireOp",EDGE,"E20.41.0"),sQuery(id+"F0.wireOp",EDGE,"E20.41.1"),sQuery(id+"F0.wireOp",EDGE,"E20.41.2"),sQuery(id+"F0.wireOp",EDGE,"E20.41.3"),sQuery(id+"F0.wireOp",EDGE,"E20.41.4"),sQuery(id+"F0.wireOp",EDGE,"E20.41.5"),sQuery(id+"F0.wireOp",EDGE,"E20.41.6"),sQuery(id+"F0.wireOp",EDGE,"E20.41.7"),sQuery(id+"F0.wireOp",EDGE,"E20.41.8"),sQuery(id+"F0.wireOp",EDGE,"E20.41.9"),sQuery(id+"F0.wireOp",EDGE,"E20.41.10"),sQuery(id+"F0.wireOp",EDGE,"E20.41.11"),sQuery(id+"F0.wireOp",EDGE,"E20.42.0"),sQuery(id+"F0.wireOp",EDGE,"E20.42.1"),sQuery(id+"F0.wireOp",EDGE,"E20.42.2"),sQuery(id+"F0.wireOp",EDGE,"E20.42.3"),sQuery(id+"F0.wireOp",EDGE,"E20.42.4"),sQuery(id+"F0.wireOp",EDGE,"E20.42.5"),sQuery(id+"F0.wireOp",EDGE,"E20.42.6"),sQuery(id+"F0.wireOp",EDGE,"E20.42.7"),sQuery(id+"F0.wireOp",EDGE,"E20.42.8"),sQuery(id+"F0.wireOp",EDGE,"E20.42.9"),sQuery(id+"F0.wireOp",EDGE,"E20.42.10"),sQuery(id+"F0.wireOp",EDGE,"E20.42.11"),sQuery(id+"F0.wireOp",EDGE,"E20.43.0"),sQuery(id+"F0.wireOp",EDGE,"E20.43.1"),sQuery(id+"F0.wireOp",EDGE,"E20.43.2"),sQuery(id+"F0.wireOp",EDGE,"E20.43.3"),sQuery(id+"F0.wireOp",EDGE,"E20.43.4"),sQuery(id+"F0.wireOp",EDGE,"E20.43.5"),sQuery(id+"F0.wireOp",EDGE,"E20.43.6"),sQuery(id+"F0.wireOp",EDGE,"E20.43.7"),sQuery(id+"F0.wireOp",EDGE,"E20.43.8"),sQuery(id+"F0.wireOp",EDGE,"E20.43.9"),sQuery(id+"F0.wireOp",EDGE,"E20.43.10"),sQuery(id+"F0.wireOp",EDGE,"E20.43.11"),sQuery(id+"F0.wireOp",EDGE,"E20.44.0"),sQuery(id+"F0.wireOp",EDGE,"E20.44.1"),sQuery(id+"F0.wireOp",EDGE,"E20.44.2"),sQuery(id+"F0.wireOp",EDGE,"E20.44.3"),sQuery(id+"F0.wireOp",EDGE,"E20.44.4"),sQuery(id+"F0.wireOp",EDGE,"E20.44.5"),sQuery(id+"F0.wireOp",EDGE,"E20.44.6"),sQuery(id+"F0.wireOp",EDGE,"E20.44.7"),sQuery(id+"F0.wireOp",EDGE,"E20.44.8"),sQuery(id+"F0.wireOp",EDGE,"E20.44.9"),sQuery(id+"F0.wireOp",EDGE,"E20.44.10"),sQuery(id+"F0.wireOp",EDGE,"E20.44.11"),sQuery(id+"F0.wireOp",EDGE,"E20.45.0"),sQuery(id+"F0.wireOp",EDGE,"E20.45.1"),sQuery(id+"F0.wireOp",EDGE,"E20.45.2"),sQuery(id+"F0.wireOp",EDGE,"E20.45.3"),sQuery(id+"F0.wireOp",EDGE,"E20.45.4"),sQuery(id+"F0.wireOp",EDGE,"E20.45.5"),sQuery(id+"F0.wireOp",EDGE,"E20.45.6"),sQuery(id+"F0.wireOp",EDGE,"E20.45.7"),sQuery(id+"F0.wireOp",EDGE,"E20.45.8"),sQuery(id+"F0.wireOp",EDGE,"E20.45.9"),sQuery(id+"F0.wireOp",EDGE,"E20.45.10"),sQuery(id+"F0.wireOp",EDGE,"E20.45.11"),sQuery(id+"F0.wireOp",EDGE,"E20.46.0"),sQuery(id+"F0.wireOp",EDGE,"E20.46.1"),sQuery(id+"F0.wireOp",EDGE,"E20.46.2"),sQuery(id+"F0.wireOp",EDGE,"E20.46.3"),sQuery(id+"F0.wireOp",EDGE,"E20.46.4"),sQuery(id+"F0.wireOp",EDGE,"E20.46.5"),sQuery(id+"F0.wireOp",EDGE,"E20.46.6"),sQuery(id+"F0.wireOp",EDGE,"E20.46.7"),sQuery(id+"F0.wireOp",EDGE,"E20.46.8"),sQuery(id+"F0.wireOp",EDGE,"E20.46.9"),sQuery(id+"F0.wireOp",EDGE,"E20.46.10"),sQuery(id+"F0.wireOp",EDGE,"E20.46.11"),sQuery(id+"F0.wireOp",EDGE,"E20.47.0"),sQuery(id+"F0.wireOp",EDGE,"E20.47.1"),sQuery(id+"F0.wireOp",EDGE,"E20.47.2"),sQuery(id+"F0.wireOp",EDGE,"E20.47.3"),sQuery(id+"F0.wireOp",EDGE,"E20.47.4"),sQuery(id+"F0.wireOp",EDGE,"E20.47.5"),sQuery(id+"F0.wireOp",EDGE,"E20.47.6"),sQuery(id+"F0.wireOp",EDGE,"E20.47.7"),sQuery(id+"F0.wireOp",EDGE,"E20.47.8"),sQuery(id+"F0.wireOp",EDGE,"E20.47.9"),sQuery(id+"F0.wireOp",EDGE,"E20.47.10"),sQuery(id+"F0.wireOp",EDGE,"E20.47.11"),sQuery(id+"F0.wireOp",EDGE,"E20.48.0"),sQuery(id+"F0.wireOp",EDGE,"E20.48.1"),sQuery(id+"F0.wireOp",EDGE,"E20.48.2"),sQuery(id+"F0.wireOp",EDGE,"E20.48.3"),sQuery(id+"F0.wireOp",EDGE,"E20.48.4"),sQuery(id+"F0.wireOp",EDGE,"E20.48.5"),sQuery(id+"F0.wireOp",EDGE,"E20.48.6"),sQuery(id+"F0.wireOp",EDGE,"E20.48.7"),sQuery(id+"F0.wireOp",EDGE,"E20.48.8"),sQuery(id+"F0.wireOp",EDGE,"E20.48.9"),sQuery(id+"F0.wireOp",EDGE,"E20.48.10"),sQuery(id+"F0.wireOp",EDGE,"E20.48.11"),sQuery(id+"F0.wireOp",EDGE,"E20.49.0"),sQuery(id+"F0.wireOp",EDGE,"E20.49.1"),sQuery(id+"F0.wireOp",EDGE,"E20.49.2"),sQuery(id+"F0.wireOp",EDGE,"E20.49.3"),sQuery(id+"F0.wireOp",EDGE,"E20.49.4"),sQuery(id+"F0.wireOp",EDGE,"E20.49.5"),sQuery(id+"F0.wireOp",EDGE,"E20.49.6"),sQuery(id+"F0.wireOp",EDGE,"E20.49.7"),sQuery(id+"F0.wireOp",EDGE,"E20.49.8"),sQuery(id+"F0.wireOp",EDGE,"E20.49.9"),sQuery(id+"F0.wireOp",EDGE,"E20.49.10"),sQuery(id+"F0.wireOp",EDGE,"E20.49.11"),sQuery(id+"F0.wireOp",EDGE,"E20.50.0"),sQuery(id+"F0.wireOp",EDGE,"E20.50.1"),sQuery(id+"F0.wireOp",EDGE,"E20.50.2"),sQuery(id+"F0.wireOp",EDGE,"E20.50.3"),sQuery(id+"F0.wireOp",EDGE,"E20.50.4"),sQuery(id+"F0.wireOp",EDGE,"E20.50.5"),sQuery(id+"F0.wireOp",EDGE,"E20.50.6"),sQuery(id+"F0.wireOp",EDGE,"E20.50.7"),sQuery(id+"F0.wireOp",EDGE,"E20.50.8"),sQuery(id+"F0.wireOp",EDGE,"E20.50.9"),sQuery(id+"F0.wireOp",EDGE,"E20.50.10"),sQuery(id+"F0.wireOp",EDGE,"E20.50.11"),sQuery(id+"F0.wireOp",EDGE,"E20.51.0"),sQuery(id+"F0.wireOp",EDGE,"E20.51.1"),sQuery(id+"F0.wireOp",EDGE,"E20.51.2"),sQuery(id+"F0.wireOp",EDGE,"E20.51.3"),sQuery(id+"F0.wireOp",EDGE,"E20.51.4"),sQuery(id+"F0.wireOp",EDGE,"E20.51.5"),sQuery(id+"F0.wireOp",EDGE,"E20.51.6"),sQuery(id+"F0.wireOp",EDGE,"E20.51.7"),sQuery(id+"F0.wireOp",EDGE,"E20.51.8"),sQuery(id+"F0.wireOp",EDGE,"E20.51.9"),sQuery(id+"F0.wireOp",EDGE,"E20.51.10"),sQuery(id+"F0.wireOp",EDGE,"E20.51.11"),sQuery(id+"F0.wireOp",EDGE,"E20.52.0"),sQuery(id+"F0.wireOp",EDGE,"E20.52.1"),sQuery(id+"F0.wireOp",EDGE,"E20.52.2"),sQuery(id+"F0.wireOp",EDGE,"E20.52.3"),sQuery(id+"F0.wireOp",EDGE,"E20.52.4"),sQuery(id+"F0.wireOp",EDGE,"E20.52.5"),sQuery(id+"F0.wireOp",EDGE,"E20.52.6"),sQuery(id+"F0.wireOp",EDGE,"E20.52.7"),sQuery(id+"F0.wireOp",EDGE,"E20.52.8"),sQuery(id+"F0.wireOp",EDGE,"E20.52.9"),sQuery(id+"F0.wireOp",EDGE,"E20.52.10"),sQuery(id+"F0.wireOp",EDGE,"E20.52.11"),sQuery(id+"F0.wireOp",EDGE,"E20.53.0"),sQuery(id+"F0.wireOp",EDGE,"E20.53.1"),sQuery(id+"F0.wireOp",EDGE,"E20.53.2"),sQuery(id+"F0.wireOp",EDGE,"E20.53.3"),sQuery(id+"F0.wireOp",EDGE,"E20.53.4"),sQuery(id+"F0.wireOp",EDGE,"E20.53.5"),sQuery(id+"F0.wireOp",EDGE,"E20.53.6"),sQuery(id+"F0.wireOp",EDGE,"E20.53.7"),sQuery(id+"F0.wireOp",EDGE,"E20.53.8"),sQuery(id+"F0.wireOp",EDGE,"E20.53.9"),sQuery(id+"F0.wireOp",EDGE,"E20.53.10"),sQuery(id+"F0.wireOp",EDGE,"E20.53.11"),sQuery(id+"F0.wireOp",EDGE,"E20.54.0"),sQuery(id+"F0.wireOp",EDGE,"E20.54.1"),sQuery(id+"F0.wireOp",EDGE,"E20.54.2"),sQuery(id+"F0.wireOp",EDGE,"E20.54.3"),sQuery(id+"F0.wireOp",EDGE,"E20.54.4"),sQuery(id+"F0.wireOp",EDGE,"E20.54.5"),sQuery(id+"F0.wireOp",EDGE,"E20.54.6"),sQuery(id+"F0.wireOp",EDGE,"E20.54.7"),sQuery(id+"F0.wireOp",EDGE,"E20.54.8"),sQuery(id+"F0.wireOp",EDGE,"E20.54.9"),sQuery(id+"F0.wireOp",EDGE,"E20.54.10"),sQuery(id+"F0.wireOp",EDGE,"E20.54.11"),sQuery(id+"F0.wireOp",EDGE,"E20.55.0"),sQuery(id+"F0.wireOp",EDGE,"E20.55.1"),sQuery(id+"F0.wireOp",EDGE,"E20.55.2"),sQuery(id+"F0.wireOp",EDGE,"E20.55.3"),sQuery(id+"F0.wireOp",EDGE,"E20.55.4"),sQuery(id+"F0.wireOp",EDGE,"E20.55.5"),sQuery(id+"F0.wireOp",EDGE,"E20.55.6"),sQuery(id+"F0.wireOp",EDGE,"E20.55.7"),sQuery(id+"F0.wireOp",EDGE,"E20.55.8"),sQuery(id+"F0.wireOp",EDGE,"E20.55.9"),sQuery(id+"F0.wireOp",EDGE,"E20.55.10"),sQuery(id+"F0.wireOp",EDGE,"E20.55.11"),sQuery(id+"F0.wireOp",EDGE,"E20.56.0"),sQuery(id+"F0.wireOp",EDGE,"E20.56.1"),sQuery(id+"F0.wireOp",EDGE,"E20.56.2"),sQuery(id+"F0.wireOp",EDGE,"E20.56.3"),sQuery(id+"F0.wireOp",EDGE,"E20.56.4"),sQuery(id+"F0.wireOp",EDGE,"E20.56.5"),sQuery(id+"F0.wireOp",EDGE,"E20.56.6"),sQuery(id+"F0.wireOp",EDGE,"E20.56.7"),sQuery(id+"F0.wireOp",EDGE,"E20.56.8"),sQuery(id+"F0.wireOp",EDGE,"E20.56.9"),sQuery(id+"F0.wireOp",EDGE,"E20.56.10"),sQuery(id+"F0.wireOp",EDGE,"E20.56.11"),sQuery(id+"F0.wireOp",EDGE,"E20.57.0"),sQuery(id+"F0.wireOp",EDGE,"E20.57.1"),sQuery(id+"F0.wireOp",EDGE,"E20.57.2"),sQuery(id+"F0.wireOp",EDGE,"E20.57.3"),sQuery(id+"F0.wireOp",EDGE,"E20.57.4"),sQuery(id+"F0.wireOp",EDGE,"E20.57.5"),sQuery(id+"F0.wireOp",EDGE,"E20.57.6"),sQuery(id+"F0.wireOp",EDGE,"E20.57.7"),sQuery(id+"F0.wireOp",EDGE,"E20.57.8"),sQuery(id+"F0.wireOp",EDGE,"E20.57.9"),sQuery(id+"F0.wireOp",EDGE,"E20.57.10"),sQuery(id+"F0.wireOp",EDGE,"E20.57.11"),sQuery(id+"F0.wireOp",EDGE,"E20.58.0"),sQuery(id+"F0.wireOp",EDGE,"E20.58.1"),sQuery(id+"F0.wireOp",EDGE,"E20.58.2"),sQuery(id+"F0.wireOp",EDGE,"E20.58.3"),sQuery(id+"F0.wireOp",EDGE,"E20.58.4"),sQuery(id+"F0.wireOp",EDGE,"E20.58.5"),sQuery(id+"F0.wireOp",EDGE,"E20.58.6"),sQuery(id+"F0.wireOp",EDGE,"E20.58.7"),sQuery(id+"F0.wireOp",EDGE,"E20.58.8"),sQuery(id+"F0.wireOp",EDGE,"E20.58.9"),sQuery(id+"F0.wireOp",EDGE,"E20.58.10"),sQuery(id+"F0.wireOp",EDGE,"E20.58.11"),sQuery(id+"F0.wireOp",EDGE,"E20.59.0"),sQuery(id+"F0.wireOp",EDGE,"E20.59.1"),sQuery(id+"F0.wireOp",EDGE,"E20.59.2"),sQuery(id+"F0.wireOp",EDGE,"E20.59.3"),sQuery(id+"F0.wireOp",EDGE,"E20.59.4"),sQuery(id+"F0.wireOp",EDGE,"E20.59.5"),sQuery(id+"F0.wireOp",EDGE,"E20.59.6"),sQuery(id+"F0.wireOp",EDGE,"E20.59.7"),sQuery(id+"F0.wireOp",EDGE,"E20.59.8"),sQuery(id+"F0.wireOp",EDGE,"E20.59.9"),sQuery(id+"F0.wireOp",EDGE,"E20.59.10"),sQuery(id+"F0.wireOp",EDGE,"E20.59.11"),sQuery(id+"F0.wireOp",EDGE,"E21.trimOffspring"),sQuery(id+"F0.wireOp",EDGE,"E22.trimOffspring"),sQuery(id+"F0.wireOp",EDGE,"E23.trimOffspring"),sQuery(id+"F0.wireOp",EDGE,"E24.trimOffspring"),sQuery(id+"F0.wireOp",EDGE,"E25.trimOffspring"),sQuery(id+"F0.wireOp",EDGE,"E26.trimOffspring"),sQuery(id+"F0.wireOp",EDGE,"E27.trimOffspring"),sQuery(id+"F0.wireOp",EDGE,"E28.trimOffspring"),sQuery(id+"F0.wireOp",EDGE,"E29.trimOffspring"),sQuery(id+"F0.wireOp",EDGE,"E30.trimOffspring"),sQuery(id+"F0.wireOp",EDGE,"E31.trimOffspring"),sQuery(id+"F0.wireOp",EDGE,"E32.trimOffspring"),sQuery(id+"F0.wireOp",EDGE,"E33.trimOffspring"),sQuery(id+"F0.wireOp",EDGE,"E34.trimOffspring"),sQuery(id+"F0.wireOp",EDGE,"E35.trimOffspring"),sQuery(id+"F0.wireOp",EDGE,"E36.trimOffspring"),sQuery(id+"F0.wireOp",EDGE,"E37.trimOffspring"),sQuery(id+"F0.wireOp",EDGE,"E38.trimOffspring"),sQuery(id+"F0.wireOp",EDGE,"E39.trimOffspring"),sQuery(id+"F0.wireOp",EDGE,"E40.trimOffspring"),sQuery(id+"F0.wireOp",EDGE,"E41.trimOffspring"),sQuery(id+"F0.wireOp",EDGE,"E42.trimOffspring"),sQuery(id+"F0.wireOp",EDGE,"E43.trimOffspring"),sQuery(id+"F0.wireOp",EDGE,"E44.trimOffspring"),sQuery(id+"F0.wireOp",EDGE,"E45.trimOffspring"),sQuery(id+"F0.wireOp",EDGE,"E46.trimOffspring"),sQuery(id+"F0.wireOp",EDGE,"E47.trimOffspring"),sQuery(id+"F0.wireOp",EDGE,"E48.trimOffspring"),sQuery(id+"F0.wireOp",EDGE,"E49.trimOffspring"),sQuery(id+"F0.wireOp",EDGE,"E50.trimOffspring"),sQuery(id+"F0.wireOp",EDGE,"E51.trimOffspring"),sQuery(id+"F0.wireOp",EDGE,"E52.trimOffspring"),sQuery(id+"F0.wireOp",EDGE,"E53.trimOffspring"),sQuery(id+"F0.wireOp",EDGE,"E54.trimOffspring"),sQuery(id+"F0.wireOp",EDGE,"E55.trimOffspring"),sQuery(id+"F0.wireOp",EDGE,"E56.trimOffspring"),sQuery(id+"F0.wireOp",EDGE,"E57.trimOffspring"),sQuery(id+"F0.wireOp",EDGE,"E58.trimOffspring"),sQuery(id+"F0.wireOp",EDGE,"E59.trimOffspring"),sQuery(id+"F0.wireOp",EDGE,"E60.trimOffspring"),sQuery(id+"F0.wireOp",EDGE,"E61.trimOffspring"),sQuery(id+"F0.wireOp",EDGE,"E62.trimOffspring"),sQuery(id+"F0.wireOp",EDGE,"E63.trimOffspring"),sQuery(id+"F0.wireOp",EDGE,"E64.trimOffspring"),sQuery(id+"F0.wireOp",EDGE,"E65.trimOffspring"),sQuery(id+"F0.wireOp",EDGE,"E66.trimOffspring"),sQuery(id+"F0.wireOp",EDGE,"E67.trimOffspring"),sQuery(id+"F0.wireOp",EDGE,"E68.trimOffspring"),sQuery(id+"F0.wireOp",EDGE,"E69.trimOffspring"),sQuery(id+"F0.wireOp",EDGE,"E70.trimOffspring"),sQuery(id+"F0.wireOp",EDGE,"E71.trimOffspring"),sQuery(id+"F0.wireOp",EDGE,"E72.trimOffspring"),sQuery(id+"F0.wireOp",EDGE,"E73.trimOffspring"),sQuery(id+"F0.wireOp",EDGE,"E74.trimOffspring"),sQuery(id+"F0.wireOp",EDGE,"E75.trimOffspring"),sQuery(id+"F0.wireOp",EDGE,"E76.trimOffspring"),sQuery(id+"F0.wireOp",EDGE,"E77.trimOffspring"),sQuery(id+"F0.wireOp",EDGE,"E78"),sQuery(id+"F0.wireOp",EDGE,"E79"),sQuery(id+"F0.wireOp",EDGE,"E80")])],"isStart":false});
            var sketch = newSketch(context, id + "F2", { "sketchPlane" : qUnion([Q0])});
            skCircle(sketch, "E81", {"center": v(0, 0) * mm, "radius": 76.4 * mm});
            skSolve(sketch);
        }
        {
            var Q0;
            Q0 = qSketchRegion(id + "F2", true);
            extrude(context, id + "F3", {"entities" : qUnion([Q0]), "operationType" : NewBodyOperationType.ADD, "depth" : 2.54 * mm});
        }
        {
            var Q0;
            Q0=makeQuery(id+"F3.boolean.opBoolean","SPLIT",FACE,{"disambiguationData":[TD([makeQuery(id+"F1.opExtrude","SWEPT_FACE",FACE,{"disambiguationData":[OSD([sQuery(id+"F0.wireOp",EDGE,"E0")])]})])],"derivedFrom":makeQuery(id+"F3.opExtrude","CAP_FACE",FACE,{"disambiguationData":[OSD([sQuery(id+"F2.wireOp",EDGE,"E81")])],"isStart":true})});
            var sketch = newSketch(context, id + "F4", { "sketchPlane" : qUnion([Q0])});
            skPoint(sketch, "E82.center", {"position": v(0, 0) * mm});
            skCircle(sketch, "E83", {"center": v(0, 42.29) * mm, "radius": 6.35 * mm});
            skCircle(sketch, "E84.1.0", {"center": v(-36.62, -21.14) * mm, "radius": 6.35 * mm});
            skCircle(sketch, "E84.2.0", {"center": v(36.62, -21.14) * mm, "radius": 6.35 * mm});
            skSolve(sketch);
        }
        {
            var Q0;
            Q0 = qSketchRegion(id + "F4", true);
            extrude(context, id + "F5", {"entities" : qUnion([Q0]), "operationType" : NewBodyOperationType.ADD, "depth" : 2.54 * mm});
        }
    });
